FCSTD DOCUMENT  (FreeCAD 0.20R29177 (Git))
Label: miniXY-Assembly
License: All rights reserved
LicenseURL: http://en.wikipedia.org/wiki/All_rights_reserved
objects: App::Link×28, PartDesign::CoordinateSystem×9, Part::FeaturePython×5, App::DocumentObjectGroup×3, App::Part×2, App::FeaturePython×1
note: 14 computed .brp shape members not serialized (recipe doc carries the construction recipe); baked Part::Feature solids carry a one-line shape summary decoded from their .brp
EXTERNAL_REF file=miniXY-Frame.FCStd obj=LCS_TopPanelOrigin
EXTERNAL_REF file=miniXY-Frame.FCStd obj=Part004
EXTERNAL_REF file=../../AppData/Local/Temp/FreeCAD/Cache/FreeCAD_Doc_34dbc569-a2dc-46c2-a682-62368ed8909b_da39a3_1616 obj=Assembly
EXTERNAL_REF file=MGN9.FCStd obj=Assembly
EXTERNAL_REF file=../../AppData/Local/Temp/FreeCAD/Cache/FreeCAD_Doc_1c5c6fb1-aa33-4595-8116-cb341c517bc9_da39a3_1616 obj=Assembly
EXTERNAL_REF file=miniXY-Frame.FCStd obj=LCS_ZLeftRailOrigin
EXTERNAL_REF file=../../AppData/Local/Temp/FreeCAD/Cache/FreeCAD_Doc_671cf0bc-0ead-4e0d-b06c-74b64cb66649_da39a3_1616 obj=LCS_Origin
EXTERNAL_REF file=../../AppData/Local/Temp/FreeCAD/Cache/FreeCAD_Doc_671cf0bc-0ead-4e0d-b06c-74b64cb66649_da39a3_1616 obj=Assembly
EXTERNAL_REF file=miniXY-Frame.FCStd obj=LCS_ZRightRailOrigin
EXTERNAL_REF file=../../AppData/Local/Temp/FreeCAD/Cache/FreeCAD_Doc_395b4d48-7136-408e-876a-f83ec305f416_da39a3_1616 obj=LCS_Origin
EXTERNAL_REF file=../../AppData/Local/Temp/FreeCAD/Cache/FreeCAD_Doc_395b4d48-7136-408e-876a-f83ec305f416_da39a3_1616 obj=Assembly
EXTERNAL_REF file=../../AppData/Local/Temp/FreeCAD/Cache/FreeCAD_Doc_015ec990-f264-4db3-840c-f19af65eb745_da39a3_1616 obj=Assembly
EXTERNAL_REF file=miniXY-XYCarriage.FCStd obj=LCS_Origin
EXTERNAL_REF file=miniXY-XYCarriage.FCStd obj=Model
EXTERNAL_REF file=Drive.FCStd obj=LCS_PullyW6T20_Origin
EXTERNAL_REF file=miniXY-XYCarriage.FCStd obj=LCS_LeftOuterIdlerPosition
EXTERNAL_REF file=Drive.FCStd obj=Part001
EXTERNAL_REF file=miniXY-XYCarriage.FCStd obj=LCS_LeftInnerIdlerPosition
EXTERNAL_REF file=miniXY-XYCarriage.FCStd obj=LCS_RightOuterIdlerPosition
EXTERNAL_REF file=miniXY-XYCarriage.FCStd obj=LCS_RightInnerIdlerPosition
EXTERNAL_REF file=miniXY-Frame.FCStd obj=LCS_StepperMountLeft
EXTERNAL_REF file=miniXY-Frame.FCStd obj=StepperMountLeft
EXTERNAL_REF file=miniXY-Frame.FCStd obj=LCS_StepperMountRightOrigin
EXTERNAL_REF file=miniXY-Frame.FCStd obj=Part015
EXTERNAL_REF file=Drive.FCStd obj=LCS_Nema17_Origin
EXTERNAL_REF file=miniXY-Frame.FCStd obj=LCS_StepperLeftOrigin
EXTERNAL_REF file=Drive.FCStd obj=Part
EXTERNAL_REF file=miniXY-Frame.FCStd obj=LCS_StepperRightOrigin
EXTERNAL_REF file=Drive.FCStd obj=LCS_DriveW6T20
EXTERNAL_REF file=miniXY-Frame.FCStd obj=LCS_DrivePullyLeftOrigin
EXTERNAL_REF file=Drive.FCStd obj=Part002
EXTERNAL_REF file=miniXY-Frame.FCStd obj=LCS_DrivePullyRightOrigin
EXTERNAL_REF file=miniXY-Frame.FCStd obj=LCS_IdlerLeftRearOrigin
EXTERNAL_REF file=miniXY-Frame.FCStd obj=LCS_IdlerLeftFrontOrigin
EXTERNAL_REF file=miniXY-Frame.FCStd obj=LCS_IdlerRightRearOrigin
EXTERNAL_REF file=miniXY-Frame.FCStd obj=LCS_IdlerRightFrontOrigin
EXTERNAL_REF file=miniXY-Frame.FCStd obj=LCS_IdlerStepperLeftOrigin
EXTERNAL_REF file=miniXY-Frame.FCStd obj=LCS_IdlerStepperRightOrigin
EXTERNAL_REF file=miniXY-Frame.FCStd obj=LCS_LeftPullyMountOrigin
EXTERNAL_REF file=miniXY-Frame.FCStd obj=LeftPullyMount
EXTERNAL_REF file=miniXY-Frame.FCStd obj=LCS_RightPullyMountOrigin
EXTERNAL_REF file=miniXY-Frame.FCStd obj=Part017
EXTERNAL_REF file=miniXY-Frame.FCStd obj=LCS_LeftPanelOrigin001
EXTERNAL_REF file=miniXY-Frame.FCStd obj=LeftPanel001
EXTERNAL_REF file=miniXY-Frame.FCStd obj=LCS_RightPanelOrigin
EXTERNAL_REF file=miniXY-Frame.FCStd obj=Part007
EXTERNAL_REF file=miniXY-Frame.FCStd obj=LCS_UpperBracketRightOrigin
EXTERNAL_REF file=miniXY-Frame.FCStd obj=Part016
EXTERNAL_REF file=miniXY-ZDrive.FCStd obj=LCS_Origin
EXTERNAL_REF file=miniXY-ZDrive.FCStd obj=Model
EXTERNAL_REF file=miniXY-PrintBed.FCStd obj=LCS_Origin
EXTERNAL_REF file=miniXY-PrintBed.FCStd obj=Model
EXTERNAL_REF file=E3D-V6-Mockup.FCStd obj=LCS_V6HotEndOrigin
EXTERNAL_REF file=E3D-V6-Mockup.FCStd obj=Part

FEATURE [PartDesign::CoordinateSystem] LCS_Origin
  AttacherType = Attacher::AttachEngine3D
  MapMode = 2
  Support = -> [X_Axis]
FEATURE [App::DocumentObjectGroup] Constraints
FEATURE [App::FeaturePython] Variables  # WARN: FeaturePython — macro-defined, semantics opaque (R4)
  GantorySpacing = 200
  PositionX = 0
  PositionY = 0
  PositionZ = -63
  Type = App::PropertyContainer
FEATURE [App::DocumentObjectGroup] Configurations
FEATURE [App::Link] TopPanel
  AssemblyType = Part::Link
  AttachedBy = #LCS_TopPanelOrigin
  AttachedTo = Parent Assembly#LCS_Origin
  LinkPlacement = pos=(0,0,0) rot=(0,-1,0;3.14159rad)
  LinkedObject = -> <external miniXY-Frame.FCStd>#Part004
  Placement = pos=(0,0,0) rot=(0,-1,0;3.14159rad)
  SolverId = Asm4EE
  expr: Placement = LCS_Origin.Placement * AttachmentOffset * miniXY_Axis#LCS_TopPanelOrigin.Placement ^ -1
FEATURE [PartDesign::CoordinateSystem] LCS_GantoryOrigin
  AttacherType = Attacher::AttachEngine3D
  MapMode = 2
  Support = -> [X_Axis001]
FEATURE [Part::FeaturePython] MGN9_Y_Left  # link proxy (typed FeaturePython)
  AttachedBy = #LCS_Origin
  AttachedTo = GantoryPositions#LCS_YLeftRailOrigin
  Length = 175
  LinkedObject = -> <external ../../AppData/Local/Temp/FreeCAD/Cache/FreeCAD_Doc_34dbc569-a2dc-46c2-a682-62368ed8909b_da39a3_1616>#Assembly
  Placement = pos=(-100,2.11e-14,-10) rot=(0.707107,0.707107,0;3.14159rad)
  Position = 0
  SolverId = Asm4EE
  SourceObject = -> <external MGN9.FCStd>#Assembly
  expr: Placement = GantoryPositions.Placement * LCS_YLeftRailOrigin.Placement * AttachmentOffset * varTmpDoc_1#LCS_Origin.Placement ^ -1
  expr: Position = <<Variables>>.PositionY
FEATURE [Part::FeaturePython] MGN9_Y_Right  # link proxy (typed FeaturePython)
  AttachedBy = #LCS_Origin
  AttachedTo = GantoryPositions#LCS_YRightRailOrigin
  Length = 175
  LinkedObject = -> <external ../../AppData/Local/Temp/FreeCAD/Cache/FreeCAD_Doc_1c5c6fb1-aa33-4595-8116-cb341c517bc9_da39a3_1616>#Assembly
  Placement = pos=(100,-2.33e-14,-10) rot=(0.707107,0.707107,0;3.14159rad)
  Position = 0
  SolverId = Asm4EE
  SourceObject = -> <external MGN9.FCStd>#Assembly
  expr: Placement = GantoryPositions.Placement * LCS_YRightRailOrigin.Placement * AttachmentOffset * varTmpDoc_2#LCS_Origin.Placement ^ -1
  expr: Position = <<Variables>>.PositionY
FEATURE [Part::FeaturePython] MGN9_Z_Left  # link proxy (typed FeaturePython)
  AttachedBy = #LCS_Origin
  AttachedTo = LeftPanel#LCS_ZLeftRailOrigin
  Length = 175
  LinkedObject = -> <external ../../AppData/Local/Temp/FreeCAD/Cache/FreeCAD_Doc_671cf0bc-0ead-4e0d-b06c-74b64cb66649_da39a3_1616>#Assembly
  Placement = pos=(-110,-15,-160) rot=(0,1,0;1.5708rad)
  Position = -63
  SolverId = Asm4EE
  SourceObject = -> <external MGN9.FCStd>#Assembly
  expr: Placement = LeftPanel.Placement * miniXY_Axis#LCS_ZLeftRailOrigin.Placement * AttachmentOffset * varTmpDoc_3#LCS_Origin.Placement ^ -1
  expr: Position = <<Variables>>.PositionZ
FEATURE [Part::FeaturePython] MGN9_Z_Right  # link proxy (typed FeaturePython)
  AttachedBy = #LCS_Origin
  AttachedTo = RightPanel#LCS_ZRightRailOrigin
  Length = 175
  LinkedObject = -> <external ../../AppData/Local/Temp/FreeCAD/Cache/FreeCAD_Doc_395b4d48-7136-408e-876a-f83ec305f416_da39a3_1616>#Assembly
  Placement = pos=(110,-15,-160) rot=(-0.707107,0,0.707107;3.14159rad)
  Position = -63
  SolverId = Asm4EE
  SourceObject = -> <external MGN9.FCStd>#Assembly
  expr: Placement = RightPanel.Placement * miniXY_Axis#LCS_ZRightRailOrigin.Placement * AttachmentOffset * varTmpDoc_4#LCS_Origin.Placement ^ -1
  expr: Position = <<Variables>>.PositionZ
FEATURE [Part::FeaturePython] MGN9_X  # link proxy (typed FeaturePython)
  AttachedBy = #LCS_Origin
  AttachedTo = GantoryPositions#LCS_XRailOrigin
  Length = 175
  LinkedObject = -> <external ../../AppData/Local/Temp/FreeCAD/Cache/FreeCAD_Doc_015ec990-f264-4db3-840c-f19af65eb745_da39a3_1616>#Assembly
  Placement = pos=(0,0,-20) rot=(0,0,1;0rad)
  Position = 0
  SolverId = Asm4EE
  SourceObject = -> <external MGN9.FCStd>#Assembly
  expr: Placement = GantoryPositions.Placement * LCS_XRailOrigin.Placement * AttachmentOffset * varTmpDoc_5#LCS_Origin.Placement ^ -1
  expr: Position = <<Variables>>.PositionX
FEATURE [App::Link] GantoryPositions  label="GantoryPositions001"
  AssemblyType = Part::Link
  AttachedBy = #LCS_GantoryOrigin
  AttachedTo = Parent Assembly#LCS_Origin
  LinkedObject = -> Part
  SolverId = Asm4EE
  expr: Placement = LCS_Origin.Placement * AttachmentOffset * LCS_GantoryOrigin.Placement ^ -1
FEATURE [PartDesign::CoordinateSystem] LCS_XRailOrigin
  AttacherType = Attacher::AttachEngine3D
  AttachmentOffset = pos=(0,0,-20) rot=(0,0,1;0rad)
  MapMode = 2
  Placement = pos=(0,0,-20) rot=(0,0,1;0rad)
  Support = -> [X_Axis001]
  expr: .AttachmentOffset.Base.y = <<Variables>>.PositionY
FEATURE [PartDesign::CoordinateSystem] LCS_YLeftRailOrigin
  AttacherType = Attacher::AttachEngine3D
  AttachmentOffset = pos=(0,-100,10) rot=(0,0,1;0rad)
  MapMode = 3
  Placement = pos=(-100,2.11e-14,-10) rot=(0.707107,0.707107,0;3.14159rad)
  Support = -> [Y_Axis001]
  expr: .AttachmentOffset.Base.y = -<<Variables>>.GantorySpacing / 2
FEATURE [PartDesign::CoordinateSystem] LCS_YRightRailOrigin
  AttacherType = Attacher::AttachEngine3D
  AttachmentOffset = pos=(0,100,10) rot=(0,0,1;0rad)
  MapMode = 3
  Placement = pos=(100,-2.33e-14,-10) rot=(0.707107,0.707107,0;3.14159rad)
  Support = -> [Y_Axis001]
  expr: .AttachmentOffset.Base.y = <<Variables>>.GantorySpacing / 2
FEATURE [App::Link] XYCarriage
  AttachedBy = #LCS_Origin
  AttachedTo = GantoryPositions#LCS_XYCarriageOrigin
  LinkPlacement = pos=(0,0,-20) rot=(1,0,0;3.14159rad)
  LinkedObject = -> <external miniXY-XYCarriage.FCStd>#Model
  Placement = pos=(0,0,-20) rot=(1,0,0;3.14159rad)
  SolverId = Asm4EE
  expr: Placement = GantoryPositions.Placement * LCS_XYCarriageOrigin.Placement * AttachmentOffset * miniXY_XYCarriage#LCS_Origin.Placement ^ -1
FEATURE [PartDesign::CoordinateSystem] LCS_XYCarriageOrigin
  AttacherType = Attacher::AttachEngine3D
  AttachmentOffset = pos=(0,0,-20) rot=(1,0,0;3.14159rad)
  MapMode = 2
  Placement = pos=(0,0,-20) rot=(1,0,0;3.14159rad)
  Support = -> [X_Axis001]
  expr: .AttachmentOffset.Base.y = <<Variables>>.PositionY
FEATURE [App::Link] IdlerCarriageLeftOuter
  AssemblyType = Part::Link
  AttachedBy = #LCS_PullyW6T20_Origin
  AttachedTo = XYCarriage#LCS_LeftOuterIdlerPosition
  LinkPlacement = pos=(-100,-1.4e-15,-31.75) rot=(1,0,0;3.14159rad)
  LinkedObject = -> <external Drive.FCStd>#Part001
  Placement = pos=(-100,-1.4e-15,-31.75) rot=(1,0,0;3.14159rad)
  SolverId = Asm4EE
  expr: Placement = XYCarriage.Placement * miniXY_XYCarriage#LCS_LeftOuterIdlerPosition.Placement * AttachmentOffset * Drive#LCS_PullyW6T20_Origin.Placement ^ -1
FEATURE [App::Link] IdlerCarriageLeftInner
  AssemblyType = Part::Link
  AttachedBy = #LCS_PullyW6T20_Origin
  AttachedTo = XYCarriage#LCS_LeftInnerIdlerPosition
  LinkPlacement = pos=(-87.27,-2.6e-15,-41.25) rot=(1,0,0;3.14159rad)
  LinkedObject = -> <external Drive.FCStd>#Part001
  Placement = pos=(-87.27,-2.6e-15,-41.25) rot=(1,0,0;3.14159rad)
  SolverId = Asm4EE
  expr: Placement = XYCarriage.Placement * miniXY_XYCarriage#LCS_LeftInnerIdlerPosition.Placement * AttachmentOffset * Drive#LCS_PullyW6T20_Origin.Placement ^ -1
FEATURE [App::Link] IdlerCarriageRightOuter
  AssemblyType = Part::Link
  AttachedBy = #LCS_PullyW6T20_Origin
  AttachedTo = XYCarriage#LCS_RightOuterIdlerPosition
  LinkPlacement = pos=(100,-2.6e-15,-41.25) rot=(1,0,0;3.14159rad)
  LinkedObject = -> <external Drive.FCStd>#Part001
  Placement = pos=(100,-2.6e-15,-41.25) rot=(1,0,0;3.14159rad)
  SolverId = Asm4EE
  expr: Placement = XYCarriage.Placement * miniXY_XYCarriage#LCS_RightOuterIdlerPosition.Placement * AttachmentOffset * Drive#LCS_PullyW6T20_Origin.Placement ^ -1
FEATURE [App::Link] IdlerCarriageRightInner
  AssemblyType = Part::Link
  AttachedBy = #LCS_PullyW6T20_Origin
  AttachedTo = XYCarriage#LCS_RightInnerIdlerPosition
  LinkPlacement = pos=(87.27,-1.4e-15,-31.75) rot=(1,0,0;3.14159rad)
  LinkedObject = -> <external Drive.FCStd>#Part001
  Placement = pos=(87.27,-1.4e-15,-31.75) rot=(1,0,0;3.14159rad)
  SolverId = Asm4EE
  expr: Placement = XYCarriage.Placement * miniXY_XYCarriage#LCS_RightInnerIdlerPosition.Placement * AttachmentOffset * Drive#LCS_PullyW6T20_Origin.Placement ^ -1
FEATURE [App::Link] StepperMountLeft
  AssemblyType = Part::Link
  AttachedBy = #LCS_StepperMountLeft
  AttachedTo = Parent Assembly#LCS_Origin
  LinkPlacement = pos=(-100,100,-46) rot=(-1,0,0;3.14159rad)
  LinkedObject = -> <external miniXY-Frame.FCStd>#StepperMountLeft
  Placement = pos=(-100,100,-46) rot=(-1,0,0;3.14159rad)
  SolverId = Asm4EE
  expr: Placement = LCS_Origin.Placement * AttachmentOffset * miniXY_Axis#LCS_StepperMountLeft.Placement ^ -1
FEATURE [App::Link] StepperMountRight
  AssemblyType = Part::Link
  AttachedBy = #LCS_StepperMountRightOrigin
  AttachedTo = Parent Assembly#LCS_Origin
  LinkPlacement = pos=(100,100,-46) rot=(-1,0,0;3.14159rad)
  LinkedObject = -> <external miniXY-Frame.FCStd>#Part015
  Placement = pos=(100,100,-46) rot=(-1,0,0;3.14159rad)
  SolverId = Asm4EE
  expr: Placement = LCS_Origin.Placement * AttachmentOffset * miniXY_Axis#LCS_StepperMountRightOrigin.Placement ^ -1
FEATURE [App::Link] StepperLeft
  AssemblyType = Part::Link
  AttachedBy = #LCS_Nema17_Origin
  AttachedTo = StepperMountLeft#LCS_StepperLeftOrigin
  LinkPlacement = pos=(-100,143.5,-51) rot=(0,0,1;0rad)
  LinkedObject = -> <external Drive.FCStd>#Part
  Placement = pos=(-100,143.5,-51) rot=(0,0,1;0rad)
  SolverId = Asm4EE
  expr: Placement = StepperMountLeft.Placement * miniXY_Axis#LCS_StepperLeftOrigin.Placement * AttachmentOffset * Drive#LCS_Nema17_Origin.Placement ^ -1
FEATURE [App::Link] StepperRight
  AssemblyType = Part::Link
  AttachedBy = #LCS_Nema17_Origin
  AttachedTo = StepperMountRight#LCS_StepperRightOrigin
  LinkPlacement = pos=(100,143.5,-51) rot=(0,0,1;0rad)
  LinkedObject = -> <external Drive.FCStd>#Part
  Placement = pos=(100,143.5,-51) rot=(0,0,1;0rad)
  SolverId = Asm4EE
  expr: Placement = StepperMountRight.Placement * miniXY_Axis#LCS_StepperRightOrigin.Placement * AttachmentOffset * Drive#LCS_Nema17_Origin.Placement ^ -1
FEATURE [App::Link] DrivePullyLeft
  AssemblyType = Part::Link
  AttachedBy = #LCS_DriveW6T20
  AttachedTo = StepperMountLeft#LCS_DrivePullyLeftOrigin
  LinkPlacement = pos=(-100,143.5,-41.25) rot=(-1,0,0;3.14159rad)
  LinkedObject = -> <external Drive.FCStd>#Part002
  Placement = pos=(-100,143.5,-41.25) rot=(-1,0,0;3.14159rad)
  SolverId = Asm4EE
  expr: Placement = StepperMountLeft.Placement * miniXY_Axis#LCS_DrivePullyLeftOrigin.Placement * AttachmentOffset * Drive#LCS_DriveW6T20.Placement ^ -1
FEATURE [App::Link] DrivePullyRight
  AssemblyType = Part::Link
  AttachedBy = #LCS_DriveW6T20
  AttachedTo = StepperMountRight#LCS_DrivePullyRightOrigin
  LinkPlacement = pos=(100,143.5,-31.75) rot=(0,0,-1;1.5708rad)
  LinkedObject = -> <external Drive.FCStd>#Part002
  Placement = pos=(100,143.5,-31.75) rot=(0,0,-1;1.5708rad)
  SolverId = Asm4EE
  expr: Placement = StepperMountRight.Placement * miniXY_Axis#LCS_DrivePullyRightOrigin.Placement * AttachmentOffset * Drive#LCS_DriveW6T20.Placement ^ -1
FEATURE [App::Link] IdlerLeftRear
  AttachedBy = #LCS_PullyW6T20_Origin
  AttachedTo = StepperMountLeft#LCS_IdlerLeftRearOrigin
  LinkPlacement = pos=(-100,100,-31.75) rot=(0,0,-1;1.5708rad)
  LinkedObject = -> <external Drive.FCStd>#Part001
  Placement = pos=(-100,100,-31.75) rot=(0,0,-1;1.5708rad)
  SolverId = Asm4EE
  expr: Placement = StepperMountLeft.Placement * miniXY_Axis#LCS_IdlerLeftRearOrigin.Placement * AttachmentOffset * Drive#LCS_PullyW6T20_Origin.Placement ^ -1
FEATURE [App::Link] IdlerLeftFront
  AttachedBy = #LCS_PullyW6T20_Origin
  AttachedTo = LeftPullyMount#LCS_IdlerLeftFrontOrigin
  LinkPlacement = pos=(-100,-100,-41.25) rot=(0,0,1;1.5708rad)
  LinkedObject = -> <external Drive.FCStd>#Part001
  Placement = pos=(-100,-100,-41.25) rot=(0,0,1;1.5708rad)
  SolverId = Asm4EE
  expr: Placement = LeftPullyMount.Placement * miniXY_Axis#LCS_IdlerLeftFrontOrigin.Placement * AttachmentOffset * Drive#LCS_PullyW6T20_Origin.Placement ^ -1
FEATURE [App::Link] IdlerRightRear
  AssemblyType = Part::Link
  AttachedBy = #LCS_PullyW6T20_Origin
  AttachedTo = StepperMountRight#LCS_IdlerRightRearOrigin
  LinkPlacement = pos=(100,100,-41.25) rot=(0,0,-1;1.5708rad)
  LinkedObject = -> <external Drive.FCStd>#Part001
  Placement = pos=(100,100,-41.25) rot=(0,0,-1;1.5708rad)
  SolverId = Asm4EE
  expr: Placement = StepperMountRight.Placement * miniXY_Axis#LCS_IdlerRightRearOrigin.Placement * AttachmentOffset * Drive#LCS_PullyW6T20_Origin.Placement ^ -1
FEATURE [App::Link] IdlerRightFront
  AttachedBy = #LCS_PullyW6T20_Origin
  AttachedTo = RightPullyMount#LCS_IdlerRightFrontOrigin
  LinkPlacement = pos=(100,-100,-31.75) rot=(0,0,1;1.5708rad)
  LinkedObject = -> <external Drive.FCStd>#Part001
  Placement = pos=(100,-100,-31.75) rot=(0,0,1;1.5708rad)
  SolverId = Asm4EE
  expr: Placement = RightPullyMount.Placement * miniXY_Axis#LCS_IdlerRightFrontOrigin.Placement * AttachmentOffset * Drive#LCS_PullyW6T20_Origin.Placement ^ -1
FEATURE [App::Link] IdlerLeftStepper
  AttachedBy = #LCS_PullyW6T20_Origin
  AttachedTo = StepperMountLeft#LCS_IdlerStepperLeftOrigin
  LinkPlacement = pos=(-87.27,112.73,-41.25) rot=(0,0,-1;1.5708rad)
  LinkedObject = -> <external Drive.FCStd>#Part001
  Placement = pos=(-87.27,112.73,-41.25) rot=(0,0,-1;1.5708rad)
  SolverId = Asm4EE
  expr: Placement = StepperMountLeft.Placement * miniXY_Axis#LCS_IdlerStepperLeftOrigin.Placement * AttachmentOffset * Drive#LCS_PullyW6T20_Origin.Placement ^ -1
FEATURE [App::Link] IdlerRightStepper
  AssemblyType = Part::Link
  AttachedBy = #LCS_PullyW6T20_Origin
  AttachedTo = StepperMountRight#LCS_IdlerStepperRightOrigin
  LinkPlacement = pos=(87.27,112.73,-31.75) rot=(0,0,-1;1.5708rad)
  LinkedObject = -> <external Drive.FCStd>#Part001
  Placement = pos=(87.27,112.73,-31.75) rot=(0,0,-1;1.5708rad)
  SolverId = Asm4EE
  expr: Placement = StepperMountRight.Placement * miniXY_Axis#LCS_IdlerStepperRightOrigin.Placement * AttachmentOffset * Drive#LCS_PullyW6T20_Origin.Placement ^ -1
FEATURE [App::Link] LeftPullyMount
  AssemblyType = Part::Link
  AttachedBy = #LCS_LeftPullyMountOrigin
  AttachedTo = Parent Assembly#LCS_Origin
  LinkPlacement = pos=(-100,-100,-60) rot=(0,-1,0;3.14159rad)
  LinkedObject = -> <external miniXY-Frame.FCStd>#LeftPullyMount
  Placement = pos=(-100,-100,-60) rot=(0,-1,0;3.14159rad)
  SolverId = Asm4EE
  expr: Placement = LCS_Origin.Placement * AttachmentOffset * miniXY_Axis#LCS_LeftPullyMountOrigin.Placement ^ -1
FEATURE [App::Link] RightPullyMount
  AssemblyType = Part::Link
  AttachedBy = #LCS_RightPullyMountOrigin
  AttachedTo = Parent Assembly#LCS_Origin
  LinkPlacement = pos=(100,-100,-60) rot=(0,-1,0;3.14159rad)
  LinkedObject = -> <external miniXY-Frame.FCStd>#Part017
  Placement = pos=(100,-100,-60) rot=(0,-1,0;3.14159rad)
  SolverId = Asm4EE
  expr: Placement = LCS_Origin.Placement * AttachmentOffset * miniXY_Axis#LCS_RightPullyMountOrigin.Placement ^ -1
FEATURE [App::Link] LeftPanel
  AssemblyType = Part::Link
  AttachedBy = #LCS_LeftPanelOrigin001
  AttachedTo = Parent Assembly#LCS_Origin
  LinkPlacement = pos=(-110,0,-60) rot=(0,1,0;1.5708rad)
  LinkedObject = -> <external miniXY-Frame.FCStd>#LeftPanel001
  Placement = pos=(-110,0,-60) rot=(0,1,0;1.5708rad)
  SolverId = Asm4EE
  expr: Placement = LCS_Origin.Placement * AttachmentOffset * miniXY_Axis#LCS_LeftPanelOrigin001.Placement ^ -1
FEATURE [App::Link] RightPanel
  AssemblyType = Part::Link
  AttachedBy = #LCS_RightPanelOrigin
  AttachedTo = Parent Assembly#LCS_Origin
  LinkPlacement = pos=(110,0,-60) rot=(0,-1,0;1.5708rad)
  LinkedObject = -> <external miniXY-Frame.FCStd>#Part007
  Placement = pos=(110,0,-60) rot=(0,-1,0;1.5708rad)
  SolverId = Asm4EE
  expr: Placement = LCS_Origin.Placement * AttachmentOffset * miniXY_Axis#LCS_RightPanelOrigin.Placement ^ -1
FEATURE [App::Link] UpperBracket
  AssemblyType = Part::Link
  AttachedBy = #LCS_UpperBracketRightOrigin
  AttachedTo = Parent Assembly#LCS_Origin
  LinkPlacement = pos=(0,110,-59) rot=(1,0,0;1.5708rad)
  LinkedObject = -> <external miniXY-Frame.FCStd>#Part016
  Placement = pos=(0,110,-59) rot=(1,0,0;1.5708rad)
  SolverId = Asm4EE
  expr: Placement = LCS_Origin.Placement * AttachmentOffset * miniXY_Axis#LCS_UpperBracketRightOrigin.Placement ^ -1
FEATURE [PartDesign::CoordinateSystem] LCS_ZDriveShaftOrigin
  AttacherType = Attacher::AttachEngine3D
  AttachmentOffset = pos=(0,-2.27,-255) rot=(0,0,1;0rad)
  MapMode = 2
  Placement = pos=(0,-2.27,-255) rot=(0,0,1;0rad)
  Support = -> [X_Axis001]
  expr: .AttachmentOffset.Base.y = 12.73 - 15
FEATURE [App::Link] ZDriveShaft
  AttachedBy = #LCS_Origin
  AttachedTo = GantoryPositions#LCS_ZDriveShaftOrigin
  LinkPlacement = pos=(0,-2.27,-255) rot=(0,0,1;0rad)
  LinkedObject = -> <external miniXY-ZDrive.FCStd>#Model
  Placement = pos=(0,-2.27,-255) rot=(0,0,1;0rad)
  SolverId = Asm4EE
  expr: Placement = GantoryPositions.Placement * LCS_ZDriveShaftOrigin.Placement * AttachmentOffset * miniXY_ZDrive#LCS_Origin.Placement ^ -1
FEATURE [App::Link] miniXY_PrintBed  label="PrintBed"
  AttachedBy = #LCS_Origin
  AttachedTo = GantoryPositions#LCS_PrintBedOrigin
  LinkPlacement = pos=(0,-15,-97) rot=(0,0,1;0rad)
  LinkedObject = -> <external miniXY-PrintBed.FCStd>#Model
  Placement = pos=(0,-15,-97) rot=(0,0,1;0rad)
  SolverId = Asm4EE
  expr: Placement = GantoryPositions.Placement * LCS_PrintBedOrigin.Placement * AttachmentOffset * miniXY_PrintBed#LCS_Origin.Placement ^ -1
FEATURE [PartDesign::CoordinateSystem] LCS_PrintBedOrigin
  AttacherType = Attacher::AttachEngine3D
  AttachmentOffset = pos=(0,-15,-97) rot=(0,0,1;0rad)
  MapMode = 2
  Placement = pos=(0,-15,-97) rot=(0,0,1;0rad)
  Support = -> [X_Axis001]
  expr: .AttachmentOffset.Base.z = -160 - Variables.PositionZ
FEATURE [App::Link] StepperZ
  LinkPlacement = pos=(45,-40,-249) rot=(0,1,0;1.5708rad)
  LinkedObject = -> <external Drive.FCStd>#Part
  Placement = pos=(45,-40,-249) rot=(0,1,0;1.5708rad)
FEATURE [PartDesign::CoordinateSystem] LCS_V6HotEndOrigin
  AttacherType = Attacher::AttachEngine3D
  AttachmentOffset = pos=(0,-20,-15) rot=(0,0,1;0rad)
  MapMode = 2
  Placement = pos=(0,-20,-15) rot=(0,0,1;0rad)
  Support = -> [X_Axis001]
  expr: .AttachmentOffset.Base.x = <<Variables>>.PositionX
  expr: .AttachmentOffset.Base.y = -20 + <<Variables>>.PositionY
FEATURE [App::Part] Part  label="GantoryPositions"
  Group = -> [LCS_GantoryOrigin,LCS_XRailOrigin,LCS_YLeftRailOrigin,LCS_YRightRailOrigin,LCS_XYCarriageOrigin,LCS_ZDriveShaftOrigin,LCS_PrintBedOrigin,LCS_V6HotEndOrigin]
  Origin = -> Origin001
FEATURE [App::DocumentObjectGroup] Parts
  Group = -> [Part]
FEATURE [App::Link] V6HotEnd
  AssemblyType = Part::Link
  AttachedBy = #LCS_V6HotEndOrigin
  AttachedTo = GantoryPositions#LCS_V6HotEndOrigin
  LinkPlacement = pos=(0,-20,-15) rot=(0,0,1;0rad)
  LinkedObject = -> <external E3D-V6-Mockup.FCStd>#Part
  Placement = pos=(0,-20,-15) rot=(0,0,1;0rad)
  SolverId = Asm4EE
  expr: Placement = GantoryPositions.Placement * LCS_V6HotEndOrigin.Placement * AttachmentOffset * E3D_V6_Mockup#LCS_V6HotEndOrigin.Placement ^ -1
FEATURE [App::Part] Model
  AssemblyType = Part::Link
  Group = -> [LCS_Origin,Constraints,Variables,Configurations,TopPanel,MGN9_Y_Left,MGN9_Y_Right,MGN9_Z_Left,MGN9_Z_Right,MGN9_X,GantoryPositions,XYCarriage,IdlerCarriageLeftOuter,IdlerCarriageLeftInner,IdlerCarriageRightOuter,IdlerCarriageRightInner,StepperMountLeft,StepperMountRight,StepperLeft,StepperRight,DrivePullyLeft,DrivePullyRight,IdlerLeftRear,IdlerLeftFront,IdlerRightRear,IdlerRightFront,+11 more]
  Origin = -> Origin
  Type = Assembly

RESOLVED EXTERNAL PARTS (link-assembly join: the EXTERNAL_REF files above that resolve inside this repo's crawl, each included once):
---- part Drive.FCStd = doc fcstd_4fe1558333d0 ----
FCSTD DOCUMENT  (FreeCAD 0.20R29177 (Git))
Label: Drive
License: All rights reserved
LicenseURL: http://en.wikipedia.org/wiki/All_rights_reserved
objects: PartDesign::Body×7, PartDesign::CoordinateSystem×7, App::Part×4, PartDesign::AdditiveBox×3, PartDesign::Chamfer×3, PartDesign::AdditiveCylinder×3, Sketcher::SketchObject×3, PartDesign::Revolution×2, PartDesign::AdditiveCone×2, PartDesign::Hole×1, PartDesign::SubtractiveCylinder×1
note: 47 computed .brp shape members not serialized (recipe doc carries the construction recipe); baked Part::Feature solids carry a one-line shape summary decoded from their .brp

FEATURE [PartDesign::AdditiveBox] Box
  AttacherType = Attacher::AttachEngine3D
  AttachmentOffset = pos=(-21,-21,0) rot=(0,0,1;0rad)
  Height = 8
  Length = 42
  MapMode = 2
  Placement = pos=(21,-21,0) rot=(0,1,0;3.14159rad)
  Support = -> [XY_Plane001]
  Width = 42
FEATURE [PartDesign::Chamfer] Chamfer
  Angle = 45
  Base = -> Box [Edge1,Edge3,Edge5,Edge7]
  BaseFeature = -> Box
  ChamferType = 0
  FlipDirection = false
  Placement = pos=(21,-21,0) rot=(0,1,0;3.14159rad)
  Size = 4
  Size2 = 1
  SupportTransform = false
  UseAllEdges = false
FEATURE [PartDesign::AdditiveBox] Box001
  AttacherType = Attacher::AttachEngine3D
  AttachmentOffset = pos=(-21,-21,0) rot=(0,0,1;0rad)
  Height = 20
  Length = 42
  MapMode = 2
  Placement = pos=(21,-21,0) rot=(0,1,0;3.14159rad)
  Support = -> [XY_Plane002]
  Width = 42
FEATURE [PartDesign::Chamfer] Chamfer001
  Angle = 45
  Base = -> Box001 [Edge1,Edge3,Edge5,Edge7]
  BaseFeature = -> Box001
  ChamferType = 0
  FlipDirection = false
  Placement = pos=(21,-21,0) rot=(0,1,0;3.14159rad)
  Size = 4
  Size2 = 1
  SupportTransform = false
  UseAllEdges = false
FEATURE [PartDesign::Body] Body001
  Group = -> [Box001,Chamfer001]
  Origin = -> Origin002
  Placement = pos=(0,0,-8) rot=(0,0,1;0rad)
  Tip = -> Chamfer001
FEATURE [PartDesign::AdditiveBox] Box002
  AttacherType = Attacher::AttachEngine3D
  AttachmentOffset = pos=(-21,-21,0) rot=(0,0,1;0rad)
  Height = 9
  Length = 42
  MapMode = 5
  Placement = pos=(21,-21,0) rot=(0,1,0;3.14159rad)
  Support = -> [XY_Plane003]
  Width = 42
FEATURE [PartDesign::Chamfer] Chamfer002
  Angle = 45
  Base = -> Box002 [Edge1,Edge3,Edge5,Edge7]
  BaseFeature = -> Box002
  ChamferType = 0
  FlipDirection = false
  Placement = pos=(21,-21,0) rot=(0,1,0;3.14159rad)
  Size = 4
  Size2 = 1
  SupportTransform = false
  UseAllEdges = false
FEATURE [PartDesign::Body] Body002
  Group = -> [Box002,Chamfer002]
  Origin = -> Origin003
  Placement = pos=(0,0,-28) rot=(0,0,1;0rad)
  Tip = -> Chamfer002
FEATURE [PartDesign::AdditiveCylinder] Cylinder
  Angle = 360
  AttacherType = Attacher::AttachEngine3D
  BaseFeature = -> Chamfer
  FirstAngle = 0
  Height = 2
  MapMode = 2
  Radius = 11
  SecondAngle = 0
  Support = -> [XY_Plane001]
FEATURE [PartDesign::AdditiveCylinder] Cylinder001
  Angle = 360
  AttacherType = Attacher::AttachEngine3D
  AttachmentOffset = pos=(0,0,2) rot=(0,0,1;0rad)
  FirstAngle = 0
  Height = 22
  MapMode = 5
  Placement = pos=(0,0,2) rot=(0,0,1;0rad)
  Radius = 2.5
  SecondAngle = 0
  Support = -> [XY_Plane004]
FEATURE [PartDesign::Body] Body003
  Group = -> [Cylinder001]
  Origin = -> Origin004
  Tip = -> Cylinder001
FEATURE [Sketcher::SketchObject] Sketch
  FullyConstrained = false
  MapMode = 5
  Support = -> [XY_Plane001]
  sketch-geometry (4):
    g0: Circle CenterX=-15.5 CenterY=15.3491 CenterZ=0 NormalX=0 NormalY=0 NormalZ=1 AngleXU=0 Radius=1.5
    g1: Circle CenterX=15.5 CenterY=15.3491 CenterZ=0 NormalX=0 NormalY=0 NormalZ=1 AngleXU=0 Radius=1.5
    g2: Circle CenterX=-15.5 CenterY=-15.3491 CenterZ=0 NormalX=0 NormalY=0 NormalZ=1 AngleXU=0 Radius=1.5
    g3: Circle CenterX=15.5 CenterY=-15.3491 CenterZ=0 NormalX=0 NormalY=0 NormalZ=1 AngleXU=0 Radius=1.5
  constraints (10):
    c: Horizontal(g0,g1)
    c: Vertical(g0,g2)
    c: Horizontal(g2,g3)
    c: Vertical(g1,g3)
    c: Symmetric(g0,g3,g-1)
    c: Equal(g0,g1)
    c: Equal(g0,g2)
    c: Equal(g0,g3)
    c: Diameter(g0) = 3
    c: DistanceX(g0,g1) = 31
FEATURE [PartDesign::Hole] Hole
  BaseFeature = -> Cylinder
  CustomThreadClearance = 0
  Depth = 5
  DepthType = 0
  Diameter = 3.4
  DrillForDepth = false
  DrillPoint = 1
  DrillPointAngle = 118
  HoleCutCountersinkAngle = 90
  HoleCutCustomValues = false
  HoleCutDepth = 0
  HoleCutDiameter = 6.1
  HoleCutType = 0
  ModelThread = false
  Profile = -> Sketch
  Tapered = false
  TaperedAngle = 90
  ThreadClass = 0
  ThreadDepth = 5
  ThreadDepthType = 0
  ThreadDirection = 0
  ThreadFit = 0
  ThreadSize = 9
  ThreadType = 1
  Threaded = false
  UseCustomThreadClearance = false
FEATURE [PartDesign::Body] Body
  Group = -> [Box,Chamfer,Cylinder,Sketch,Hole]
  Origin = -> Origin001
  Tip = -> Hole
FEATURE [Sketcher::SketchObject] Sketch001
  FullyConstrained = true
  MapMode = 5
  Placement = pos=(0,0,0) rot=(1,0,0;1.5708rad)
  Support = -> [XZ_Plane006]
  sketch-geometry (8):
    g0: LineSegment StartX=2.5 StartY=4.25 StartZ=0 EndX=2.5 EndY=-4.25 EndZ=0
    g1: LineSegment StartX=2.5 StartY=-4.25 StartZ=0 EndX=9 EndY=-4.25 EndZ=0
    g2: LineSegment StartX=9 StartY=-4.25 StartZ=0 EndX=9 EndY=-3.25 EndZ=0
    g3: LineSegment StartX=9 StartY=-3.25 StartZ=0 EndX=6.365 EndY=-3.25 EndZ=0
    g4: LineSegment StartX=6.365 StartY=-3.25 StartZ=0 EndX=6.365 EndY=3.25 EndZ=0
    g5: LineSegment StartX=6.365 StartY=3.25 StartZ=0 EndX=9 EndY=3.25 EndZ=0
    g6: LineSegment StartX=9 StartY=3.25 StartZ=0 EndX=9 EndY=4.25 EndZ=0
    g7: LineSegment StartX=9 StartY=4.25 StartZ=0 EndX=2.5 EndY=4.25 EndZ=0
  constraints (21):
    c: Coincident(g0,g1)
    c: Horizontal(g1)
    c: Coincident(g1,g2)
    c: Coincident(g2,g3)
    c: Coincident(g3,g4)
    c: Coincident(g4,g5)
    c: Horizontal(g5)
    c: Coincident(g5,g6)
    c: Coincident(g6,g7)
    c: Coincident(g7,g0)
    c: Horizontal(g7)
    c: Symmetric(g0,g0,g-1)
    c: Symmetric(g4,g3,g-1)
    c: Vertical(g6)
    c: Vertical(g2)
    c: Symmetric(g2,g5,g-1)
    c: DistanceX(g-1,g4) = 6.365
    c: DistanceX(g-1,g0) = 2.5
    c: DistanceY(g6,g6) = 1
    c: DistanceX(g-1,g6) = 9
    c: DistanceY(g3,g4) = 6.5
FEATURE [PartDesign::Revolution] Revolution
  Angle = 360
  Axis = (0,-2e-16,1)
  Base = (0,0,0)
  Placement = pos=(0,0,0) rot=(1,0,0;1.5708rad)
  Profile = -> Sketch001
  ReferenceAxis = -> Sketch001 [V_Axis]
FEATURE [PartDesign::Body] Body004
  Group = -> [Sketch001,Revolution]
  Origin = -> Origin006
  Tip = -> Revolution
FEATURE [PartDesign::CoordinateSystem] LCS_Nema17_Origin
  AttacherType = Attacher::AttachEngine3D
  MapMode = 2
  Support = -> [X_Axis]
FEATURE [App::Part] Part  label="Nema17"
  Group = -> [Body,Body001,Body002,Body003,LCS_Nema17_Origin]
  Origin = -> Origin
FEATURE [PartDesign::CoordinateSystem] LCS_PullyW6T20_Origin  label="LCS_IdlerW6T20_Origin"
  AttacherType = Attacher::AttachEngine3D
  MapMode = 2
  Support = -> [X_Axis005]
FEATURE [PartDesign::CoordinateSystem] LCS_PullyW6T20_Left  label="LCS_IdlerW6T20_Left"
  AttacherType = Attacher::AttachEngine3D
  AttachmentOffset = pos=(6.365,0,0) rot=(0,0,1;0rad)
  MapMode = 2
  Placement = pos=(6.365,0,0) rot=(0,0,1;0rad)
  Support = -> [LCS_PullyW6T20_Origin]
FEATURE [PartDesign::CoordinateSystem] LCS_PullyW6T20_Right  label="LCS_IdlerW6T20_Right"
  AttacherType = Attacher::AttachEngine3D
  AttachmentOffset = pos=(-6.365,0,0) rot=(0,0,1;0rad)
  MapMode = 2
  Placement = pos=(-6.365,0,0) rot=(0,0,1;0rad)
  Support = -> [LCS_PullyW6T20_Origin]
FEATURE [PartDesign::CoordinateSystem] LCS_PullyW6T20_Front  label="LCS_IdlerW6T20_Front"
  AttacherType = Attacher::AttachEngine3D
  AttachmentOffset = pos=(0,-6.365,0) rot=(0,0,1;0rad)
  MapMode = 2
  Placement = pos=(0,-6.365,0) rot=(0,0,1;0rad)
  Support = -> [LCS_PullyW6T20_Origin]
FEATURE [PartDesign::CoordinateSystem] LCS_PullyW6T20_Rear
  AttacherType = Attacher::AttachEngine3D
  AttachmentOffset = pos=(0,6.365,0) rot=(0,0,1;0rad)
  MapMode = 2
  Placement = pos=(0,6.365,0) rot=(0,0,1;0rad)
  Support = -> [LCS_PullyW6T20_Origin]
FEATURE [App::Part] Part001  label="IdlerW6T20"
  Group = -> [Body004,LCS_PullyW6T20_Origin,LCS_PullyW6T20_Left,LCS_PullyW6T20_Right,LCS_PullyW6T20_Front,LCS_PullyW6T20_Rear]
  Origin = -> Origin005
FEATURE [Sketcher::SketchObject] Sketch002
  FullyConstrained = true
  MapMode = 5
  Placement = pos=(0,0,0) rot=(1,0,0;1.5708rad)
  Support = -> [XZ_Plane008]
  sketch-geometry (8):
    g0: LineSegment StartX=2.5 StartY=4.9 StartZ=0 EndX=2.5 EndY=-11.1 EndZ=0
    g1: LineSegment StartX=2.5 StartY=-11.1 StartZ=0 EndX=8 EndY=-11.1 EndZ=0
    g2: LineSegment StartX=8 StartY=-11.1 StartZ=0 EndX=8 EndY=-3.6 EndZ=0
    g3: LineSegment StartX=8 StartY=-3.6 StartZ=0 EndX=6.365 EndY=-3.6 EndZ=0
    g4: LineSegment StartX=6.365 StartY=-3.6 StartZ=0 EndX=6.365 EndY=3.6 EndZ=0
    g5: LineSegment StartX=6.365 StartY=3.6 StartZ=0 EndX=8 EndY=3.6 EndZ=0
    g6: LineSegment StartX=8 StartY=3.6 StartZ=0 EndX=8 EndY=4.9 EndZ=0
    g7: LineSegment StartX=8 StartY=4.9 StartZ=0 EndX=2.5 EndY=4.9 EndZ=0
  constraints (23):
    c: Vertical(g0)
    c: Coincident(g0,g1)
    c: Coincident(g1,g2)
    c: Vertical(g2)
    c: Coincident(g2,g3)
    c: Coincident(g3,g4)
    c: Coincident(g4,g5)
    c: Horizontal(g5)
    c: Coincident(g5,g6)
    c: Vertical(g6)
    c: Coincident(g6,g7)
    c: Horizontal(g7)
    c: Coincident(g7,g0)
    c: Horizontal(g1)
    c: Horizontal(g3)
    c: DistanceX(g-1,g0) = 2.5
    c: DistanceY(g6,g6) = 1.3
    c: DistanceY(g4,g4) = 7.2
    c: DistanceY(g2,g2) = 7.5
    c: Symmetric(g4,g3,g-1)
    c: DistanceX(g-1,g4) = 6.365
    c: DistanceX(g-1,g1) = 8
    c: DistanceX(g-1,g6) = 8
FEATURE [PartDesign::Revolution] Revolution001
  Angle = 360
  Axis = (0,-2e-16,1)
  Base = (0,0,0)
  Placement = pos=(0,0,0) rot=(1,0,0;1.5708rad)
  Profile = -> Sketch002
  ReferenceAxis = -> Sketch002 [V_Axis]
FEATURE [PartDesign::Body] Body005
  Group = -> [Sketch002,Revolution001]
  Origin = -> Origin008
  Tip = -> Revolution001
FEATURE [PartDesign::CoordinateSystem] LCS_DriveW6T20
  AttacherType = Attacher::AttachEngine3D
  MapMode = 2
  Support = -> [X_Axis007]
FEATURE [App::Part] Part002  label="DriveW6T20"
  Group = -> [Body005,LCS_DriveW6T20]
  Origin = -> Origin007
FEATURE [PartDesign::AdditiveCylinder] Cylinder002
  Angle = 360
  AttacherType = Attacher::AttachEngine3D
  FirstAngle = 0
  Height = 8.5
  MapMode = 5
  Radius = 5.99
  SecondAngle = 0
  Support = -> [XY_Plane010]
FEATURE [PartDesign::AdditiveCone] Cone
  Angle = 360
  AttacherType = Attacher::AttachEngine3D
  BaseFeature = -> Cylinder002
  Height = 2
  MapMode = 5
  Radius1 = 7.1
  Radius2 = 5.1
  Support = -> [XY_Plane010]
FEATURE [PartDesign::AdditiveCone] Cone001
  Angle = 360
  AttacherType = Attacher::AttachEngine3D
  AttachmentOffset = pos=(0,0,-8.5) rot=(0,0,1;0rad)
  BaseFeature = -> Cone
  Height = 2
  MapMode = 5
  Placement = pos=(0,0,8.5) rot=(0,1,0;3.14159rad)
  Radius1 = 7.1
  Radius2 = 5.1
  Support = -> [XY_Plane010]
FEATURE [PartDesign::SubtractiveCylinder] Cylinder003
  Angle = 360
  AttacherType = Attacher::AttachEngine3D
  BaseFeature = -> Cone001
  FirstAngle = 0
  Height = 13
  MapMode = 5
  Radius = 4
  SecondAngle = 0
  Support = -> [XY_Plane010]
FEATURE [PartDesign::Body] Body006
  Group = -> [Cylinder002,Cone,Cone001,Cylinder003]
  Origin = -> Origin010
  Tip = -> Cylinder003
FEATURE [App::Part] Part003  label="Pully2GT20TSmooth"
  Group = -> [Body006]
  Origin = -> Origin009
---- part MGN9.FCStd = doc fcstd_087b5e8fa0dc ----
FCSTD DOCUMENT  (FreeCAD 0.20R29177 (Git))
Label: MGN9
License: All rights reserved
LicenseURL: http://en.wikipedia.org/wiki/All_rights_reserved
objects: PartDesign::Chamfer×7, PartDesign::Pad×6, PartDesign::Body×6, Sketcher::SketchObject×5, PartDesign::ShapeBinder×5, PartDesign::CoordinateSystem×4, App::DocumentObjectGroup×3, App::Part×3, PartDesign::Hole×2, App::Link×2, App::FeaturePython×1
note: 50 computed .brp shape members not serialized (recipe doc carries the construction recipe); baked Part::Feature solids carry a one-line shape summary decoded from their .brp

FEATURE [Sketcher::SketchObject] Sketch
  FullyConstrained = true
  MapMode = 5
  Placement = pos=(0,0,0) rot=(1,0,0;1.5708rad)
  Support = -> [XZ_Plane001]
  sketch-geometry (8):
    g0: LineSegment StartX=-4.5 StartY=6.5 StartZ=0 EndX=4.5 EndY=6.5 EndZ=0
    g1: LineSegment StartX=4.5 StartY=6.5 StartZ=0 EndX=4.5 EndY=5.5 EndZ=0
    g2: LineSegment StartX=4.5 StartY=0 StartZ=0 EndX=-4.5 EndY=0 EndZ=0
    g3: LineSegment StartX=-4.5 StartY=0 StartZ=0 EndX=-4.5 EndY=3.5 EndZ=0
    g4: ArcOfCircle CenterX=-4.5 CenterY=4.5 CenterZ=0 NormalX=0 NormalY=0 NormalZ=1 AngleXU=0 Radius=1 StartAngle=4.71239 EndAngle=7.85398
    g5: LineSegment StartX=-4.5 StartY=5.5 StartZ=0 EndX=-4.5 EndY=6.5 EndZ=0
    g6: ArcOfCircle CenterX=4.5 CenterY=4.5 CenterZ=0 NormalX=0 NormalY=0 NormalZ=1 AngleXU=0 Radius=1 StartAngle=1.5708 EndAngle=4.71239
    g7: LineSegment StartX=4.5 StartY=3.5 StartZ=0 EndX=4.5 EndY=0 EndZ=0
  constraints (22):
    c: Coincident(g0,g1)
    c: Coincident(g7,g2)
    c: Coincident(g2,g3)
    c: Coincident(g5,g0)
    c: Symmetric(g2,g7,g-2)
    c: Symmetric(g0,g0,g-2)
    c: Vertical(g3)
    c: DistanceX(g2,g2) = 9
    c: DistanceY(g3,g5) = 6.5
    c: PointOnObject(g2,g-1)
    c: PointOnObject(g4,g3)
    c: DistanceY(g-1,g4) = 4.5
    c: Radius(g4) = 1
    c: Coincident(g3,g4)
    c: Coincident(g5,g4)
    c: Vertical(g5)
    c: Vertical(g4,g3)
    c: PointOnObject(g6,g1)
    c: Coincident(g1,g6)
    c: Coincident(g7,g6)
    c: Symmetric(g4,g6,g-2)
    c: Symmetric(g3,g6,g-2)
FEATURE [Sketcher::SketchObject] Sketch001  label="UnitSketch"
  FullyConstrained = true
  MapMode = 5
  Placement = pos=(0,0,0) rot=(1,0,0;1.5708rad)
  Support = -> [XZ_Plane002]
  sketch-geometry (12):
    g0: LineSegment StartX=-10 StartY=8 StartZ=0 EndX=-4 EndY=8 EndZ=0
    g1: LineSegment StartX=10 StartY=8 StartZ=0 EndX=10 EndY=0 EndZ=0
    g2: LineSegment StartX=10 StartY=0 StartZ=0 EndX=4.5 EndY=0 EndZ=0
    g3: LineSegment StartX=-10 StartY=0 StartZ=0 EndX=-10 EndY=8 EndZ=0
    g4: LineSegment StartX=-4.5 StartY=4.5 StartZ=0 EndX=4.5 EndY=4.5 EndZ=0
    g5: LineSegment StartX=4.5 StartY=4.5 StartZ=0 EndX=4.5 EndY=0 EndZ=0
    g6: LineSegment StartX=-4.5 StartY=0 StartZ=0 EndX=-4.5 EndY=4.5 EndZ=0
    g7: LineSegment StartX=-4.5 StartY=0 StartZ=0 EndX=-10 EndY=0 EndZ=0
    g8: LineSegment StartX=4 StartY=8 StartZ=0 EndX=4 EndY=7.55 EndZ=0
    g9: LineSegment StartX=4 StartY=7.55 StartZ=0 EndX=-4 EndY=7.55 EndZ=0
    g10: LineSegment StartX=-4 StartY=7.55 StartZ=0 EndX=-4 EndY=8 EndZ=0
    g11: LineSegment StartX=4 StartY=8 StartZ=0 EndX=10 EndY=8 EndZ=0
  constraints (31):
    c: Coincident(g11,g1)
    c: Coincident(g1,g2)
    c: Coincident(g7,g3)
    c: Coincident(g3,g0)
    c: Symmetric(g7,g1,g-2)
    c: Symmetric(g0,g11,g-2)
    c: PointOnObject(g7,g-1)
    c: DistanceX(g7,g2) = 20
    c: DistanceY(g3,g3) = 8
    c: Vertical(g3)
    c: Coincident(g4,g5)
    c: Coincident(g6,g4)
    c: Horizontal(g4)
    c: Vertical(g5)
    c: Vertical(g6)
    c: Coincident(g2,g5)
    c: DistanceX(g6,g5) = 9
    c: DistanceY(g6,g6) = 4.5
    c: Symmetric(g6,g2,g-2)
    c: Coincident(g8,g9)
    c: Coincident(g9,g10)
    c: Coincident(g10,g0)
    c: Coincident(g8,g11)
    c: Symmetric(g0,g8,g-2)
    c: DistanceX(g9,g9) = 8
    c: Horizontal(g0)
    c: DistanceY(g10,g10) = 0.45
    c: Symmetric(g9,g8,g-2)
    c: Vertical(g10)
    c: Coincident(g7,g6)
    c: PointOnObject(g6,g-1)
FEATURE [Sketcher::SketchObject] Sketch002  label="CoverSketch"
  FullyConstrained = true
  MapMode = 5
  Placement = pos=(0,0,0) rot=(1,0,0;1.5708rad)
  Support = -> [XZ_Plane002]
  sketch-geometry (12):
    g0: LineSegment StartX=9.85 StartY=7.65 StartZ=0 EndX=9.85 EndY=0 EndZ=0
    g1: LineSegment StartX=9.85 StartY=0 StartZ=0 EndX=4.5 EndY=0 EndZ=0
    g2: LineSegment StartX=-9.85 StartY=0 StartZ=0 EndX=-9.85 EndY=7.65 EndZ=0
    g3: LineSegment StartX=-4.5 StartY=4.5 StartZ=0 EndX=4.5 EndY=4.5 EndZ=0
    g4: LineSegment StartX=4.5 StartY=4.5 StartZ=0 EndX=4.5 EndY=3.5 EndZ=0
    g5: LineSegment StartX=-4.5 StartY=0 StartZ=0 EndX=-4.5 EndY=1.5 EndZ=0
    g6: LineSegment StartX=-9.85 StartY=7.65 StartZ=0 EndX=9.85 EndY=7.65 EndZ=0
    g7: LineSegment StartX=-4.5 StartY=0 StartZ=0 EndX=-9.85 EndY=0 EndZ=0
    g8: ArcOfCircle CenterX=-4.5 CenterY=2.5 CenterZ=0 NormalX=0 NormalY=0 NormalZ=1 AngleXU=0 Radius=1 StartAngle=4.71239 EndAngle=7.85398
    g9: ArcOfCircle CenterX=4.5 CenterY=2.5 CenterZ=0 NormalX=0 NormalY=0 NormalZ=1 AngleXU=0 Radius=1 StartAngle=1.5708 EndAngle=4.71239
    g10: LineSegment StartX=-4.5 StartY=3.5 StartZ=0 EndX=-4.5 EndY=4.5 EndZ=0
    g11: LineSegment StartX=4.5 StartY=1.5 StartZ=0 EndX=4.5 EndY=0 EndZ=0
  constraints (32):
    c: Coincident(g6,g0)
    c: Coincident(g0,g1)
    c: Coincident(g7,g2)
    c: Vertical(g2)
    c: Coincident(g3,g4)
    c: Coincident(g10,g3)
    c: Vertical(g5)
    c: Coincident(g1,g11)
    c: Coincident(g5,g7)
    c: Symmetric(g2,g0,g-2)
    c: Symmetric(g5,g1,g-2)
    c: Symmetric(g3,g3,g-2)
    c: PointOnObject(g5,g-1)
    c: PointOnObject(g2,g-1)
    c: DistanceX(g3,g3) = 9
    c: DistanceY(g5,g10) = 4.5
    c: DistanceY(g2,g2) = 7.65
    c: Coincident(g6,g2)
    c: DistanceX(g6,g6) = 19.7
    c: Symmetric(g2,g0,g-2)
    c: PointOnObject(g8,g5)
    c: PointOnObject(g9,g4)
    c: Coincident(g5,g8)
    c: Coincident(g10,g8)
    c: Coincident(g4,g9)
    c: Coincident(g11,g9)
    c: Vertical(g8,g5)
    c: Vertical(g10)
    c: Symmetric(g8,g4,g-2)
    c: Symmetric(g9,g5,g-2)
    c: DistanceY(g5,g8) = 2.5
    c: Radius(g8) = 1
FEATURE [PartDesign::CoordinateSystem] LCS_Origin
  AttacherType = Attacher::AttachEngine3D
  MapMode = 2
  Support = -> [X_Axis008]
FEATURE [App::FeaturePython] Variables  # WARN: FeaturePython — macro-defined, semantics opaque (R4)
  Length = 100
  Position = 0
  Type = App::PropertyContainer
FEATURE [App::DocumentObjectGroup] Constraints
FEATURE [App::DocumentObjectGroup] Configurations
FEATURE [PartDesign::Pad] Pad
  Direction = (0,-1,-2e-16)
  Length = 100
  Length2 = 10
  Midplane = true
  Placement = pos=(0,0,0) rot=(1,0,0;1.5708rad)
  Profile = -> Sketch
  ReferenceAxis = -> Sketch [N_Axis]
  Type = 0
  expr: Length = <<Variables>>.Length
FEATURE [PartDesign::ShapeBinder] ShapeBinder
  Placement = pos=(0,0,0) rot=(1,0,0;1.5708rad)
  Support = -> [Sketch001]
  TraceSupport = false
FEATURE [PartDesign::Pad] Pad001
  Direction = (0,1,2e-16)
  Length = 18.9
  Length2 = 10
  Midplane = true
  Placement = pos=(0,0,0) rot=(1,0,0;1.5708rad)
  Profile = -> ShapeBinder
  Type = 0
FEATURE [PartDesign::ShapeBinder] ShapeBinder001
  Placement = pos=(0,0,0) rot=(1,0,0;1.5708rad)
  Support = -> [Sketch002]
  TraceSupport = false
FEATURE [PartDesign::Pad] Pad002
  Direction = (0,1,2e-16)
  Length = 4
  Length2 = 10
  Placement = pos=(0,0,0) rot=(1,0,0;1.5708rad)
  Profile = -> ShapeBinder001
  Type = 0
FEATURE [PartDesign::ShapeBinder] ShapeBinder002
  Placement = pos=(0,0,0) rot=(1,0,0;1.5708rad)
  Support = -> [Sketch002]
  TraceSupport = false
FEATURE [PartDesign::Pad] Pad003
  Direction = (0,1,2e-16)
  Length = 4
  Length2 = 10
  Placement = pos=(0,0,0) rot=(1,0,0;1.5708rad)
  Profile = -> ShapeBinder002
  Reversed = true
  Type = 0
FEATURE [PartDesign::Chamfer] Chamfer
  Angle = 45
  Base = -> Pad003 [Edge5,Edge8,Edge11,Edge2]
  BaseFeature = -> Pad003
  ChamferType = 0
  FlipDirection = false
  Placement = pos=(0,0,0) rot=(1,0,0;1.5708rad)
  Size = 1
  Size2 = 1
  SupportTransform = false
  UseAllEdges = false
FEATURE [PartDesign::Chamfer] Chamfer001
  Angle = 45
  Base = -> Pad001 [Edge5,Edge20,Edge23,Edge2]
  BaseFeature = -> Pad001
  ChamferType = 0
  FlipDirection = false
  Placement = pos=(0,0,0) rot=(1,0,0;1.5708rad)
  Size = 0.5
  Size2 = 1
  SupportTransform = false
  UseAllEdges = false
FEATURE [PartDesign::Chamfer] Chamfer002
  Angle = 45
  Base = -> Pad002 [Edge8,Edge5,Edge2,Edge11]
  BaseFeature = -> Pad002
  ChamferType = 0
  FlipDirection = false
  Placement = pos=(0,0,0) rot=(1,0,0;1.5708rad)
  Size = 1
  Size2 = 1
  SupportTransform = false
  UseAllEdges = false
FEATURE [PartDesign::Body] Body002  label="Returner001"
  Group = -> [ShapeBinder001,Pad002,Chamfer002]
  Origin = -> Origin004
  Placement = pos=(0,9.4,0) rot=(0,0,1;0rad)
  Tip = -> Chamfer002
FEATURE [PartDesign::Chamfer] Chamfer003
  Angle = 45
  Base = -> Pad [Edge2,Edge11,Edge14,Edge1]
  BaseFeature = -> Pad
  ChamferType = 0
  FlipDirection = false
  Placement = pos=(0,0,0) rot=(1,0,0;1.5708rad)
  Size = 0.35
  Size2 = 1
  SupportTransform = false
  UseAllEdges = false
FEATURE [PartDesign::ShapeBinder] ShapeBinder003
  Placement = pos=(0,0,0) rot=(1,0,0;1.5708rad)
  Support = -> [Sketch002]
  TraceSupport = false
FEATURE [PartDesign::Pad] Pad004
  Direction = (0,1,2e-16)
  Length = 1
  Length2 = 10
  Placement = pos=(0,0,0) rot=(1,0,0;1.5708rad)
  Profile = -> ShapeBinder003
  Type = 0
FEATURE [PartDesign::Chamfer] Chamfer004
  Angle = 45
  Base = -> Pad004 [Edge8,Edge5,Edge11,Edge2]
  BaseFeature = -> Pad004
  ChamferType = 0
  FlipDirection = false
  Placement = pos=(0,0,0) rot=(1,0,0;1.5708rad)
  Size = 1
  Size2 = 1
  SupportTransform = false
  UseAllEdges = false
FEATURE [PartDesign::Body] Body004  label="wiper001"
  Group = -> [ShapeBinder003,Pad004,Chamfer004]
  Origin = -> Origin006
  Placement = pos=(0,13.4,0) rot=(0,0,1;0rad)
  Tip = -> Chamfer004
FEATURE [PartDesign::ShapeBinder] ShapeBinder004
  Placement = pos=(0,0,0) rot=(1,0,0;1.5708rad)
  Support = -> [Sketch002]
  TraceSupport = false
FEATURE [PartDesign::Pad] Pad005
  Direction = (0,1,2e-16)
  Length = 1
  Length2 = 10
  Placement = pos=(0,0,0) rot=(1,0,0;1.5708rad)
  Profile = -> ShapeBinder004
  Reversed = true
  Type = 0
FEATURE [PartDesign::Chamfer] Chamfer005
  Angle = 45
  Base = -> Pad003 [Edge8,Edge11,Edge5,Edge2]
  BaseFeature = -> Pad003
  ChamferType = 0
  FlipDirection = false
  Placement = pos=(0,0,0) rot=(1,0,0;1.5708rad)
  Size = 1
  Size2 = 1
  SupportTransform = false
  UseAllEdges = false
FEATURE [PartDesign::Body] Body003  label="Returner002"
  Group = -> [ShapeBinder002,Pad003,Chamfer,Chamfer005]
  Origin = -> Origin005
  Placement = pos=(0,-9.4,0) rot=(0,0,1;0rad)
  Tip = -> Chamfer005
FEATURE [PartDesign::Chamfer] Chamfer006
  Angle = 45
  Base = -> Pad005 [Edge5,Edge2,Edge8,Edge11]
  BaseFeature = -> Pad005
  ChamferType = 0
  FlipDirection = false
  Placement = pos=(0,0,0) rot=(1,0,0;1.5708rad)
  Size = 1
  Size2 = 1
  SupportTransform = false
  UseAllEdges = false
FEATURE [PartDesign::Body] Body005  label="wiper002"
  Group = -> [ShapeBinder004,Pad005,Chamfer006]
  Origin = -> Origin007
  Placement = pos=(0,-13.4,0) rot=(0,0,1;0rad)
  Tip = -> Chamfer006
FEATURE [Sketcher::SketchObject] Sketch003
  FullyConstrained = true
  MapMode = 5
  Placement = pos=(0,1.8e-15,8) rot=(0,0,1;3.14159rad)
  Support = -> [Chamfer001]
  sketch-geometry (4):
    g0: Circle CenterX=-7.5 CenterY=5 CenterZ=0 NormalX=0 NormalY=0 NormalZ=1 AngleXU=0 Radius=1.5
    g1: Circle CenterX=7.5 CenterY=5 CenterZ=0 NormalX=0 NormalY=0 NormalZ=1 AngleXU=0 Radius=1.5
    g2: Circle CenterX=-7.5 CenterY=-5 CenterZ=0 NormalX=0 NormalY=0 NormalZ=1 AngleXU=0 Radius=1.5
    g3: Circle CenterX=7.5 CenterY=-5 CenterZ=0 NormalX=0 NormalY=0 NormalZ=1 AngleXU=0 Radius=1.5
  constraints (9):
    c: Symmetric(g0,g2,g-1)
    c: Symmetric(g0,g1,g-2)
    c: Symmetric(g2,g3,g-2)
    c: DistanceY(g2,g0) = 10
    c: DistanceX(g0,g1) = 15
    c: Equal(g0,g1)
    c: Equal(g0,g2)
    c: Equal(g0,g3)
    c: Diameter(g0) = 3
FEATURE [PartDesign::Hole] Hole
  BaseFeature = -> Chamfer001
  CustomThreadClearance = 0
  Depth = 4.4
  DepthType = 0
  Diameter = 2.5
  DrillForDepth = false
  DrillPoint = 1
  DrillPointAngle = 118
  HoleCutCountersinkAngle = 90
  HoleCutCustomValues = false
  HoleCutDepth = 0
  HoleCutDiameter = 6.1
  HoleCutType = 0
  ModelThread = false
  Placement = pos=(0,0,0) rot=(1,0,0;1.5708rad)
  Profile = -> Sketch003
  Tapered = false
  TaperedAngle = 90
  ThreadClass = 0
  ThreadDepth = 4.4
  ThreadDepthType = 0
  ThreadDirection = 0
  ThreadFit = 0
  ThreadSize = 9
  ThreadType = 1
  Threaded = true
  UseCustomThreadClearance = false
FEATURE [PartDesign::Body] Body001  label="UnitBody"
  Group = -> [ShapeBinder,Pad001,Chamfer001,Sketch003,Hole]
  Origin = -> Origin003
  Tip = -> Hole
FEATURE [PartDesign::CoordinateSystem] LCS_RailPartOrigin
  AttacherType = Attacher::AttachEngine3D
  MapMode = 3
  Placement = pos=(0,0,0) rot=(0,0,-1;1.5708rad)
  Support = -> [Y_Axis]
FEATURE [PartDesign::CoordinateSystem] LCS_RailPartTop
  AttacherType = Attacher::AttachEngine3D
  AttachmentOffset = pos=(0,0,6.5) rot=(0,0,1;0rad)
  MapMode = 3
  Placement = pos=(-7e-16,7e-16,6.5) rot=(0,0,-1;1.5708rad)
  Support = -> [Y_Axis]
FEATURE [PartDesign::CoordinateSystem] LCS_UnitPartOrigin
  AttacherType = Attacher::AttachEngine3D
  AttachmentOffset = pos=(0,0,4.5) rot=(0,0,1;0rad)
  MapMode = 3
  Placement = pos=(-5e-16,5e-16,4.5) rot=(0,0,-1;1.5708rad)
  Support = -> [Y_Axis002]
FEATURE [App::Part] Part001  label="Unit"
  Group = -> [Sketch001,Sketch002,Body001,Body002,Body003,Body004,Body005,LCS_UnitPartOrigin]
  Origin = -> Origin002
FEATURE [App::Link] Rail  label="Rail001"
  AssemblyType = Part::Link
  AttachedBy = #LCS_RailPartOrigin
  AttachedTo = Parent Assembly#LCS_Origin
  LinkPlacement = pos=(0,0,0) rot=(0,0,1;1.5708rad)
  LinkedObject = -> Part
  Placement = pos=(0,0,0) rot=(0,0,1;1.5708rad)
  SolverId = Asm4EE
  expr: Placement = LCS_Origin.Placement * AttachmentOffset * LCS_RailPartOrigin.Placement ^ -1
FEATURE [App::Link] Unit  label="Unit001"
  AssemblyType = Part::Link
  AttachedBy = #LCS_UnitPartOrigin
  AttachedTo = Rail#LCS_RailPartTop
  LinkPlacement = pos=(0,0,2) rot=(0,0,1;1.5708rad)
  LinkedObject = -> Part001
  Placement = pos=(0,0,2) rot=(0,0,1;1.5708rad)
  SolverId = Asm4EE
  expr: .AttachmentOffset.Base.x = <<Variables>>.Position
  expr: Placement = Rail.Placement * LCS_RailPartTop.Placement * AttachmentOffset * LCS_UnitPartOrigin.Placement ^ -1
FEATURE [App::Part] Assembly
  AssemblyType = Part::Link
  Group = -> [LCS_Origin,Variables,Constraints,Configurations,Rail,Unit]
  Origin = -> Origin008
  Type = Assembly
FEATURE [Sketcher::SketchObject] Sketch004
  AttachmentOffset = pos=(0,0,-6.5) rot=(0,0,1;0rad)
  FullyConstrained = true
  MapMode = 3
  Placement = pos=(-7e-16,7e-16,6.5) rot=(0.707107,0.707107,0;3.14159rad)
  Support = -> [Y_Axis001]
  sketch-geometry (19):
    g0: Circle CenterX=0 CenterY=0 CenterZ=0 NormalX=0 NormalY=0 NormalZ=1 AngleXU=0 Radius=1.5
    g1: Circle CenterX=-20 CenterY=0 CenterZ=0 NormalX=0 NormalY=0 NormalZ=1 AngleXU=0 Radius=1.5
    g2: Circle CenterX=-40 CenterY=0 CenterZ=0 NormalX=0 NormalY=0 NormalZ=1 AngleXU=0 Radius=1.5
    g3: Circle CenterX=-60 CenterY=0 CenterZ=0 NormalX=0 NormalY=0 NormalZ=1 AngleXU=0 Radius=1.5
    g4: Circle CenterX=-80 CenterY=0 CenterZ=0 NormalX=0 NormalY=0 NormalZ=1 AngleXU=0 Radius=1.5
    g5: Circle CenterX=-100 CenterY=0 CenterZ=0 NormalX=0 NormalY=0 NormalZ=1 AngleXU=0 Radius=1.5
    g6: Circle CenterX=-120 CenterY=0 CenterZ=0 NormalX=0 NormalY=0 NormalZ=1 AngleXU=0 Radius=1.5
    g7: Circle CenterX=-140 CenterY=0 CenterZ=0 NormalX=0 NormalY=0 NormalZ=1 AngleXU=0 Radius=1.5
    g8: Circle CenterX=-160 CenterY=0 CenterZ=0 NormalX=0 NormalY=0 NormalZ=1 AngleXU=0 Radius=1.5
    g9: Circle CenterX=-180 CenterY=0 CenterZ=0 NormalX=0 NormalY=0 NormalZ=1 AngleXU=0 Radius=1.5
    g10: Circle CenterX=20 CenterY=0 CenterZ=0 NormalX=0 NormalY=0 NormalZ=1 AngleXU=0 Radius=1.5
    g11: Circle CenterX=40 CenterY=0 CenterZ=0 NormalX=0 NormalY=0 NormalZ=1 AngleXU=0 Radius=1.5
    g12: Circle CenterX=60 CenterY=0 CenterZ=0 NormalX=0 NormalY=0 NormalZ=1 AngleXU=0 Radius=1.5
    g13: Circle CenterX=80 CenterY=0 CenterZ=0 NormalX=0 NormalY=0 NormalZ=1 AngleXU=0 Radius=1.5
    g14: Circle CenterX=100 CenterY=0 CenterZ=0 NormalX=0 NormalY=0 NormalZ=1 AngleXU=0 Radius=1.5
    g15: Circle CenterX=120 CenterY=0 CenterZ=0 NormalX=0 NormalY=0 NormalZ=1 AngleXU=0 Radius=1.5
    g16: Circle CenterX=140 CenterY=0 CenterZ=0 NormalX=0 NormalY=0 NormalZ=1 AngleXU=0 Radius=1.5
    g17: Circle CenterX=160 CenterY=0 CenterZ=0 NormalX=0 NormalY=0 NormalZ=1 AngleXU=0 Radius=1.5
    g18: Circle CenterX=180 CenterY=0 CenterZ=0 NormalX=0 NormalY=0 NormalZ=1 AngleXU=0 Radius=1.5
  constraints (30):
    c: PointOnObject(g1,g-1)
    c: PointOnObject(g2,g-1)
    c: PointOnObject(g3,g-1)
    c: PointOnObject(g4,g-1)
    c: PointOnObject(g5,g-1)
    c: PointOnObject(g6,g-1)
    c: PointOnObject(g7,g-1)
    c: PointOnObject(g8,g-1)
    c: PointOnObject(g9,g-1)
    c: Equal(g0, g1-g18) x18
    c: Diameter(g0) = 3
    c: Symmetric(g9,g18,g-2)
    c: Symmetric(g8,g17,g-2)
    c: DistanceX(g9,g8) = 20
    c: Symmetric(g7,g16,g-2)
    c: DistanceX(g8,g7) = 20
    c: Symmetric(g6,g15,g-2)
    c: DistanceX(g7,g6) = 20
    c: Symmetric(g14,g5,g-2)
    c: DistanceX(g6,g5) = 20
    c: Symmetric(g4,g13,g-2)
    c: DistanceX(g5,g4) = 20
    c: Symmetric(g12,g3,g-2)
    c: DistanceX(g4,g3) = 20
    c: Symmetric(g11,g2,g-2)
    c: DistanceX(g3,g2) = 20
    c: Symmetric(g10,g1,g-2)
    c: DistanceX(g2,g1) = 20
    c: DistanceX(g1,g0) = 20
    c: Coincident(g0,g-1)
FEATURE [PartDesign::Hole] Hole001
  BaseFeature = -> Chamfer003
  CustomThreadClearance = 0
  Depth = 733.603
  DepthType = 1
  Diameter = 3.7
  DrillForDepth = false
  DrillPoint = 1
  DrillPointAngle = 118
  HoleCutCountersinkAngle = 90
  HoleCutCustomValues = false
  HoleCutDepth = 3.06
  HoleCutDiameter = 6.1
  HoleCutType = 1
  ModelThread = false
  Placement = pos=(0,0,0) rot=(1,0,0;1.5708rad)
  Profile = -> Sketch004
  Reversed = true
  Tapered = false
  TaperedAngle = 90
  ThreadClass = 0
  ThreadDepth = 733.603
  ThreadDepthType = 0
  ThreadDirection = 0
  ThreadFit = 0
  ThreadSize = 0
  ThreadType = 0
  Threaded = false
  UseCustomThreadClearance = false
FEATURE [PartDesign::Body] Body  label="RailBody"
  Group = -> [Sketch,Pad,Sketch004,Chamfer003,Hole001]
  Origin = -> Origin001
  Tip = -> Hole001
FEATURE [App::Part] Part  label="Rail"
  Group = -> [Body,LCS_RailPartOrigin,LCS_RailPartTop]
  Origin = -> Origin
FEATURE [App::DocumentObjectGroup] Parts
  Group = -> [Part,Part001]
---- part miniXY-Frame.FCStd = doc fcstd_6a076cb3e2fe (504191 chars; too large to inline — full recipe in that document) ----
---- part miniXY-PrintBed.FCStd = doc fcstd_e5c5c3b6efab ----
FCSTD DOCUMENT  (FreeCAD 0.20R29177 (Git))
Label: miniXY-PrintBed
License: All rights reserved
LicenseURL: http://en.wikipedia.org/wiki/All_rights_reserved
objects: Sketcher::SketchObject×7, PartDesign::Pad×7, PartDesign::Body×7, PartDesign::CoordinateSystem×3, App::DocumentObjectGroup×3, App::Part×3, App::Link×2, App::FeaturePython×1
note: 31 computed .brp shape members not serialized (recipe doc carries the construction recipe); baked Part::Feature solids carry a one-line shape summary decoded from their .brp

FEATURE [PartDesign::CoordinateSystem] LCS_Origin
  AttacherType = Attacher::AttachEngine3D
  MapMode = 2
  Support = -> [X_Axis]
FEATURE [App::DocumentObjectGroup] Constraints
FEATURE [App::FeaturePython] Variables  # WARN: FeaturePython — macro-defined, semantics opaque (R4)
  BedSize = 150
  BedThickness = 7
  GantorySpacing = 200
  Type = App::PropertyContainer
FEATURE [App::DocumentObjectGroup] Configurations
FEATURE [Sketcher::SketchObject] Sketch
  FullyConstrained = true
  MapMode = 5
  Support = -> [XY_Plane002]
  expr: Constraints[10] = <<Variables>>.BedSize
  sketch-geometry (4):
    g0: LineSegment StartX=-75 StartY=75 StartZ=0 EndX=75 EndY=75 EndZ=0
    g1: LineSegment StartX=75 StartY=75 StartZ=0 EndX=75 EndY=-75 EndZ=0
    g2: LineSegment StartX=75 StartY=-75 StartZ=0 EndX=-75 EndY=-75 EndZ=0
    g3: LineSegment StartX=-75 StartY=-75 StartZ=0 EndX=-75 EndY=75 EndZ=0
  constraints (11):
    c: Coincident(g0,g1)
    c: Coincident(g1,g2)
    c: Coincident(g2,g3)
    c: Coincident(g3,g0)
    c: Horizontal(g0)
    c: Horizontal(g2)
    c: Vertical(g1)
    c: Vertical(g3)
    c: Symmetric(g0,g1,g-1)
    c: Equal(g0,g3)
    c: Distance(g3) = 150
FEATURE [PartDesign::Pad] Pad
  Direction = (0,0,1)
  Length = 7
  Length2 = 10
  Profile = -> Sketch
  ReferenceAxis = -> Sketch [N_Axis]
  Type = 0
  expr: Length = <<Variables>>.BedThickness
FEATURE [PartDesign::Body] Body  label="Bed"
  Group = -> [Sketch,Pad]
  Origin = -> Origin002
  Tip = -> Pad
FEATURE [Sketcher::SketchObject] Sketch001
  AttachmentOffset = pos=(0,0,7) rot=(0,0,1;0rad)
  FullyConstrained = false
  MapMode = 5
  Placement = pos=(0,0,7) rot=(0,0,1;0rad)
  Support = -> [XY_Plane003]
  expr: .AttachmentOffset.Base.z = <<Variables>>.BedThickness
  expr: Constraints[12] = <<Variables>>.BedSize / 2 - 15
  expr: Constraints[9] = <<Variables>>.BedSize
  sketch-geometry (5):
    g0: LineSegment StartX=-75 StartY=58.3105 StartZ=0 EndX=75 EndY=58.3105 EndZ=0
    g1: LineSegment StartX=75 StartY=58.3105 StartZ=0 EndX=75 EndY=-58.3105 EndZ=0
    g2: LineSegment StartX=75 StartY=-58.3105 StartZ=0 EndX=-75 EndY=-58.3105 EndZ=0
    g3: LineSegment StartX=-75 StartY=-58.3105 StartZ=0 EndX=-75 EndY=91.6895 EndZ=0
    g4: Circle CenterX=0 CenterY=60 CenterZ=0 NormalX=0 NormalY=0 NormalZ=1 AngleXU=0 Radius=6
  constraints (13):
    c: Coincident(g0,g1)
    c: Coincident(g1,g2)
    c: Coincident(g2,g3)
    c: Horizontal(g0)
    c: Horizontal(g2)
    c: Vertical(g1)
    c: Vertical(g3)
    c: Symmetric(g0,g1,g-1)
    c: Equal(g0,g3)
    c: Distance(g3) = 150
    c: PointOnObject(g4,g-2)
    c: Diameter(g4) = 12
    c: DistanceY(g4) = 60
FEATURE [Sketcher::SketchObject] Sketch002
  AttachmentOffset = pos=(0,0,7) rot=(0,0,1;0rad)
  FullyConstrained = true
  MapMode = 5
  Placement = pos=(0,0,7) rot=(0,0,1;0rad)
  Support = -> [XY_Plane004]
  expr: .AttachmentOffset.Base.z = <<Variables>>.BedThickness
  expr: Constraints[10] = <<Variables>>.BedSize
  expr: Constraints[11] = -(<<Variables>>.BedSize / 2 - 15)
  expr: Constraints[12] = -(<<Variables>>.BedSize / 2 - 15)
  sketch-geometry (5):
    g0: LineSegment StartX=-75 StartY=75 StartZ=0 EndX=75 EndY=75 EndZ=0
    g1: LineSegment StartX=75 StartY=75 StartZ=0 EndX=75 EndY=-75 EndZ=0
    g2: LineSegment StartX=75 StartY=-75 StartZ=0 EndX=-75 EndY=-75 EndZ=0
    g3: LineSegment StartX=-75 StartY=-75 StartZ=0 EndX=-75 EndY=75 EndZ=0
    g4: Circle CenterX=-60 CenterY=-60 CenterZ=0 NormalX=0 NormalY=0 NormalZ=1 AngleXU=0 Radius=6
  constraints (14):
    c: Coincident(g0,g1)
    c: Coincident(g1,g2)
    c: Coincident(g2,g3)
    c: Coincident(g3,g0)
    c: Horizontal(g0)
    c: Horizontal(g2)
    c: Vertical(g1)
    c: Vertical(g3)
    c: Symmetric(g1,g0,g-1)
    c: Equal(g0,g3)
    c: Distance(g3) = 150
    c: DistanceY(g4) = -60
    c: DistanceX(g4) = -60
    c: Diameter(g4) = 12
FEATURE [Sketcher::SketchObject] Sketch003
  AttachmentOffset = pos=(0,0,7) rot=(0,0,1;0rad)
  FullyConstrained = true
  MapMode = 5
  Placement = pos=(0,0,7) rot=(0,0,1;0rad)
  Support = -> [XY_Plane005]
  expr: .AttachmentOffset.Base.z = <<Variables>>.BedThickness
  expr: Constraints[10] = <<Variables>>.BedSize
  expr: Constraints[11] = <<Variables>>.BedSize / 2 - 15
  expr: Constraints[12] = -(<<Variables>>.BedSize / 2 - 15)
  sketch-geometry (5):
    g0: LineSegment StartX=-75 StartY=75 StartZ=0 EndX=75 EndY=75 EndZ=0
    g1: LineSegment StartX=75 StartY=75 StartZ=0 EndX=75 EndY=-75 EndZ=0
    g2: LineSegment StartX=75 StartY=-75 StartZ=0 EndX=-75 EndY=-75 EndZ=0
    g3: LineSegment StartX=-75 StartY=-75 StartZ=0 EndX=-75 EndY=75 EndZ=0
    g4: Circle CenterX=60 CenterY=-60 CenterZ=0 NormalX=0 NormalY=0 NormalZ=1 AngleXU=0 Radius=6
  constraints (14):
    c: Coincident(g0,g1)
    c: Coincident(g1,g2)
    c: Coincident(g2,g3)
    c: Coincident(g3,g0)
    c: Horizontal(g0)
    c: Horizontal(g2)
    c: Vertical(g1)
    c: Vertical(g3)
    c: Symmetric(g0,g1,g-1)
    c: Equal(g0,g3)
    c: Distance(g3) = 150
    c: DistanceX(g4) = 60
    c: DistanceY(g4) = -60
    c: Diameter(g4) = 12
FEATURE [PartDesign::Pad] Pad001
  Direction = (0,0,1)
  Length = 10
  Length2 = 10
  Profile = -> Sketch001
  ReferenceAxis = -> Sketch001 [N_Axis]
  Type = 0
FEATURE [PartDesign::Body] Body001  label="BootRear"
  Group = -> [Sketch001,Pad001]
  Origin = -> Origin003
  Tip = -> Pad001
FEATURE [PartDesign::Pad] Pad002
  Direction = (0,0,1)
  Length = 10
  Length2 = 10
  Profile = -> Sketch002
  ReferenceAxis = -> Sketch002 [N_Axis]
  Type = 0
FEATURE [PartDesign::Body] Body002  label="BootFrontLeft"
  Group = -> [Sketch002,Pad002]
  Origin = -> Origin004
  Tip = -> Pad002
FEATURE [PartDesign::Pad] Pad003
  Direction = (0,0,1)
  Length = 10
  Length2 = 10
  Profile = -> Sketch003
  ReferenceAxis = -> Sketch003 [N_Axis]
  Type = 0
FEATURE [PartDesign::Body] Body003  label="BootFrontRight"
  Group = -> [Sketch003,Pad003]
  Origin = -> Origin005
  Tip = -> Pad003
FEATURE [Sketcher::SketchObject] Sketch004
  FullyConstrained = true
  MapMode = 5
  Placement = pos=(0,0,0) rot=(0.57735,0.57735,0.57735;2.0944rad)
  Support = -> [YZ_Plane006]
  expr: Constraints[11] = -(<<Variables>>.BedSize / 2 - 15)
  expr: Constraints[12] = 10 + <<Variables>>.BedThickness
  sketch-geometry (5):
    g0: LineSegment StartX=-65 StartY=27 StartZ=0 EndX=-55 EndY=27 EndZ=0
    g1: LineSegment StartX=-55 StartY=27 StartZ=0 EndX=-55 EndY=17 EndZ=0
    g2: LineSegment StartX=-55 StartY=17 StartZ=0 EndX=-65 EndY=17 EndZ=0
    g3: LineSegment StartX=-65 StartY=17 StartZ=0 EndX=-65 EndY=27 EndZ=0
    g4: GeomPoint X=-60 Y=22 Z=0
  constraints (13):
    c: Coincident(g0,g1)
    c: Coincident(g1,g2)
    c: Coincident(g2,g3)
    c: Coincident(g3,g0)
    c: Horizontal(g0)
    c: Horizontal(g2)
    c: Vertical(g1)
    c: Vertical(g3)
    c: Equal(g0,g3)
    c: Distance(g3) = 10
    c: Symmetric(g0,g1,g4)
    c: DistanceX(g4) = -60
    c: DistanceY(g2) = 17
FEATURE [PartDesign::Pad] Pad004
  Direction = (1,-2e-16,3e-16)
  Length = 200
  Length2 = 10
  Midplane = true
  Placement = pos=(0,0,0) rot=(0.57735,0.57735,0.57735;2.0944rad)
  Profile = -> Sketch004
  ReferenceAxis = -> Sketch004 [N_Axis]
  Type = 0
  expr: Length = Variables.GantorySpacing
FEATURE [PartDesign::Body] Body004  label="FrameFront"
  Group = -> [Sketch004,Pad004]
  Origin = -> Origin006
  Tip = -> Pad004
FEATURE [Sketcher::SketchObject] Sketch005
  FullyConstrained = true
  MapMode = 5
  Placement = pos=(0,0,0) rot=(0.57735,0.57735,0.57735;2.0944rad)
  Support = -> [YZ_Plane007]
  expr: Constraints[11] = <<Variables>>.BedSize / 2 - 15
  expr: Constraints[12] = 10 + <<Variables>>.BedThickness
  sketch-geometry (5):
    g0: LineSegment StartX=55 StartY=27 StartZ=0 EndX=65 EndY=27 EndZ=0
    g1: LineSegment StartX=65 StartY=27 StartZ=0 EndX=65 EndY=17 EndZ=0
    g2: LineSegment StartX=65 StartY=17 StartZ=0 EndX=55 EndY=17 EndZ=0
    g3: LineSegment StartX=55 StartY=17 StartZ=0 EndX=55 EndY=27 EndZ=0
    g4: GeomPoint X=60 Y=22 Z=0
  constraints (13):
    c: Coincident(g0,g1)
    c: Coincident(g1,g2)
    c: Coincident(g2,g3)
    c: Coincident(g3,g0)
    c: Horizontal(g0)
    c: Horizontal(g2)
    c: Vertical(g1)
    c: Vertical(g3)
    c: Symmetric(g0,g1,g4)
    c: Equal(g0,g3)
    c: Distance(g3) = 10
    c: DistanceX(g4) = 60
    c: DistanceY(g2) = 17
FEATURE [PartDesign::Pad] Pad005
  Direction = (1,-2e-16,3e-16)
  Length = 200
  Length2 = 10
  Midplane = true
  Placement = pos=(0,0,0) rot=(0.57735,0.57735,0.57735;2.0944rad)
  Profile = -> Sketch005
  ReferenceAxis = -> Sketch005 [N_Axis]
  Type = 0
  expr: Length = <<Variables>>.GantorySpacing
FEATURE [PartDesign::Body] Body005  label="FrameRear"
  Group = -> [Sketch005,Pad005]
  Origin = -> Origin007
  Tip = -> Pad005
FEATURE [Sketcher::SketchObject] Sketch006
  AttachmentOffset = pos=(0,0,100) rot=(0,0,1;0rad)
  FullyConstrained = true
  MapMode = 5
  Placement = pos=(100,-2.22e-14,2.22e-14) rot=(0.57735,0.57735,0.57735;2.0944rad)
  Support = -> [YZ_Plane008]
  expr: .AttachmentOffset.Base.z = Variables.GantorySpacing / 2
  sketch-geometry (20):
    g0: LineSegment StartX=10 StartY=12.5 StartZ=0 EndX=10 EndY=-12.5 EndZ=0
    g1: LineSegment StartX=-10 StartY=-12.5 StartZ=0 EndX=-10 EndY=12.5 EndZ=0
    g2: ArcOfCircle CenterX=-7.5 CenterY=12.5 CenterZ=0 NormalX=0 NormalY=0 NormalZ=1 AngleXU=0 Radius=2.5 StartAngle=1.5708 EndAngle=3.14159
    g3: GeomPoint X=-10 Y=15 Z=0
    g4: ArcOfCircle CenterX=-7.5 CenterY=-12.5 CenterZ=0 NormalX=0 NormalY=0 NormalZ=1 AngleXU=0 Radius=2.5 StartAngle=3.14159 EndAngle=4.71239
    g5: GeomPoint X=-10 Y=-15 Z=0
    g6: ArcOfCircle CenterX=7.5 CenterY=-12.5 CenterZ=0 NormalX=0 NormalY=0 NormalZ=1 AngleXU=0 Radius=2.5 StartAngle=4.71239 EndAngle=6.28319
    g7: GeomPoint X=10 Y=-15 Z=0
    g8: ArcOfCircle CenterX=7.5 CenterY=12.5 CenterZ=0 NormalX=0 NormalY=0 NormalZ=1 AngleXU=0 Radius=2.5 StartAngle=0 EndAngle=1.5708
    g9: GeomPoint X=10 Y=15 Z=0
    g10: ArcOfCircle CenterX=0 CenterY=12.5 CenterZ=0 NormalX=0 NormalY=0 NormalZ=1 AngleXU=0 Radius=6 StartAngle=0.562536 EndAngle=2.57906
    g11: ArcOfCircle CenterX=-6.34429 CenterY=16.5 CenterZ=0 NormalX=0 NormalY=0 NormalZ=1 AngleXU=0 Radius=1.5 StartAngle=4.71239 EndAngle=5.72065
    g12: ArcOfCircle CenterX=6.34429 CenterY=16.5 CenterZ=0 NormalX=0 NormalY=0 NormalZ=1 AngleXU=0 Radius=1.5 StartAngle=3.70413 EndAngle=4.71239
    g13: ArcOfCircle CenterX=0 CenterY=-12.5 CenterZ=0 NormalX=0 NormalY=0 NormalZ=1 AngleXU=0 Radius=6 StartAngle=3.70413 EndAngle=5.72065
    g14: ArcOfCircle CenterX=-6.34429 CenterY=-16.5 CenterZ=0 NormalX=0 NormalY=0 NormalZ=1 AngleXU=0 Radius=1.5 StartAngle=0.562536 EndAngle=1.5708
    g15: ArcOfCircle CenterX=6.34429 CenterY=-16.5 CenterZ=0 NormalX=0 NormalY=0 NormalZ=1 AngleXU=0 Radius=1.5 StartAngle=1.5708 EndAngle=2.57906
    g16: LineSegment StartX=-7.5 StartY=15 StartZ=0 EndX=-6.34429 EndY=15 EndZ=0
    g17: LineSegment StartX=6.34429 StartY=15 StartZ=0 EndX=7.5 EndY=15 EndZ=0
    g18: LineSegment StartX=-6.34429 StartY=-15 StartZ=0 EndX=-7.5 EndY=-15 EndZ=0
    g19: LineSegment StartX=7.5 StartY=-15 StartZ=0 EndX=6.34429 EndY=-15 EndZ=0
  constraints (46):
    c: Vertical(g0)
    c: Vertical(g1)
    c: Symmetric(g3,g7,g-1)
    c: PointOnObject(g3,g1)
    c: Tangent(g16,g2) = 1.5708
    c: Tangent(g1,g2) = 1.5708
    c: PointOnObject(g5,g1)
    c: Tangent(g1,g4) = 1.5708
    c: Tangent(g18,g4) = 1.5708
    c: PointOnObject(g7,g0)
    c: Tangent(g19,g6) = 1.5708
    c: Tangent(g0,g6) = 1.5708
    c: PointOnObject(g9,g0)
    c: Tangent(g0,g8) = 1.5708
    c: Tangent(g17,g8) = 1.5708
    c: Equal(g2,g4)
    c: Radius(g2) = 2.5
    c: Tangent(g10,g11) = 1.5708
    c: Tangent(g10,g12) = 1.5708
    c: PointOnObject(g10,g-2)
    c: Horizontal(g16)
    c: PointOnObject(g3,g16)
    c: Horizontal(g17)
    c: PointOnObject(g9,g17)
    c: Tangent(g11,g16) = -1.5708
    c: Tangent(g12,g17) = -1.5708
    c: Diameter(g10) = 12
    c: Equal(g11,g12)
    c: Diameter(g11) = 3
    c: Tangent(g14,g13) = 1.5708
    c: Tangent(g13,g15) = 1.5708
    c: Horizontal(g18)
    c: PointOnObject(g5,g18)
    c: Horizontal(g19)
    c: PointOnObject(g7,g19)
    c: Tangent(g14,g18) = -1.5708
    c: Symmetric(g13,g10,g-1)
    c: Tangent(g15,g19) = -1.5708
    c: Equal(g14,g11)
    c: Equal(g15,g11)
    c: Equal(g13,g10)
    c: DistanceY(g5,g3) = 30
    c: DistanceX(g3,g9) = 20
    c: Symmetric(g2,g8,g-2)
    c: Symmetric(g6,g4,g-2)
    c: DistanceY(g13,g10) = 25
FEATURE [PartDesign::Pad] Pad006
  Direction = (1,-2e-16,3e-16)
  Length = 10
  Length2 = 10
  Placement = pos=(0,0,0) rot=(0.57735,0.57735,0.57735;2.0944rad)
  Profile = -> Sketch006
  ReferenceAxis = -> Sketch006 [N_Axis]
  Reversed = true
  Type = 0
FEATURE [PartDesign::Body] Body006  label="CarriageLeftBase"
  Group = -> [Sketch006,Pad006]
  Origin = -> Origin008
  Tip = -> Pad006
FEATURE [PartDesign::CoordinateSystem] LCS_PrintBedOrigin
  AttacherType = Attacher::AttachEngine3D
  AttachmentOffset = pos=(0,0,-22) rot=(0,0,-1;1.5708rad)
  MapMode = 3
  Placement = pos=(-2.4e-15,2.4e-15,22) rot=(0,1,0;3.14159rad)
  Support = -> [Y_Axis001]
FEATURE [App::Part] Part  label="PrintBed"
  Group = -> [Body,Body001,Body002,Body003,Body004,Body005,LCS_PrintBedOrigin]
  Origin = -> Origin001
FEATURE [App::Link] PrintBed  label="PrintBed001"
  AssemblyType = Part::Link
  AttachedBy = #LCS_PrintBedOrigin
  AttachedTo = Parent Assembly#LCS_Origin
  LinkPlacement = pos=(1e-16,0,22) rot=(0,-1,0;3.14159rad)
  LinkedObject = -> Part
  Placement = pos=(1e-16,0,22) rot=(0,-1,0;3.14159rad)
  SolverId = Asm4EE
  expr: Placement = LCS_Origin.Placement * AttachmentOffset * LCS_PrintBedOrigin.Placement ^ -1
FEATURE [App::Link] CarriageLeft  label="CarriageLeft001"
  AttachedBy = #LCS_CarriageLeftOrigin
  AttachedTo = Parent Assembly#LCS_Origin
  LinkPlacement = pos=(0,0,0) rot=(0,-1,0;3.14159rad)
  LinkedObject = -> Part001
  Placement = pos=(0,0,0) rot=(0,-1,0;3.14159rad)
  SolverId = Asm4EE
  expr: Placement = LCS_Origin.Placement * AttachmentOffset * LCS_CarriageLeftOrigin.Placement ^ -1
FEATURE [App::Part] Model
  Group = -> [LCS_Origin,Constraints,Variables,Configurations,PrintBed,CarriageLeft]
  Origin = -> Origin
  Type = Assembly
FEATURE [PartDesign::CoordinateSystem] LCS_CarriageLeftOrigin
  AttacherType = Attacher::AttachEngine3D
  AttachmentOffset = pos=(0,0,0) rot=(0,0,-1;1.5708rad)
  MapMode = 3
  Placement = pos=(0,0,0) rot=(0,1,0;3.14159rad)
  Support = -> [Y_Axis009]
FEATURE [App::Part] Part001  label="CarriageLeft"
  Group = -> [Body006,LCS_CarriageLeftOrigin]
  Origin = -> Origin009
FEATURE [App::DocumentObjectGroup] Parts
  Group = -> [Part,Part001]
---- part miniXY-XYCarriage.FCStd = doc fcstd_459d2d5a2655 ----
FCSTD DOCUMENT  (FreeCAD 0.20R29177 (Git))
Label: miniXY-XYCarriage
License: All rights reserved
LicenseURL: http://en.wikipedia.org/wiki/All_rights_reserved
objects: PartDesign::CoordinateSystem×10, Sketcher::SketchObject×10, PartDesign::Body×9, PartDesign::Pad×7, PartDesign::Boolean×7, App::Part×5, PartDesign::AdditivePrism×4, PartDesign::ShapeBinder×4, App::DocumentObjectGroup×3, App::Link×3, PartDesign::Hole×2, Part::FeaturePython×2, App::FeaturePython×1, PartDesign::AdditiveLoft×1
note: 70 computed .brp shape members not serialized (recipe doc carries the construction recipe); baked Part::Feature solids carry a one-line shape summary decoded from their .brp

FEATURE [PartDesign::Body] Body001  label="CarriageBaseBrace"
  Origin = -> Origin002
FEATURE [PartDesign::Body] Body003  label="CarriageLeftBrace"
  Origin = -> Origin005
FEATURE [PartDesign::CoordinateSystem] LCS_Origin
  AttacherType = Attacher::AttachEngine3D
  MapMode = 2
  Support = -> [X_Axis006]
FEATURE [App::DocumentObjectGroup] Constraints
FEATURE [App::FeaturePython] Variables  # WARN: FeaturePython — macro-defined, semantics opaque (R4)
  CarriageThickness = 7
  GantorySpacing = 200
  IdlerDiameter = 12.73
  IdlerHeight = 8.5
  Type = App::PropertyContainer
  WasherThickness = 0.5
FEATURE [App::DocumentObjectGroup] Configurations
FEATURE [PartDesign::CoordinateSystem] LCS_CarriageLeftPosition
  AttacherType = Attacher::AttachEngine3D
  AttachmentOffset = pos=(-100,0,0) rot=(0,0,1;0rad)
  MapMode = 2
  Placement = pos=(-100,0,0) rot=(0,0,1;0rad)
  Support = -> [X_Axis014]
  expr: .AttachmentOffset.Base.x = -<<Variables>>.GantorySpacing / 2
FEATURE [PartDesign::CoordinateSystem] LCS_CarriageRightPosition
  AttacherType = Attacher::AttachEngine3D
  AttachmentOffset = pos=(100,0,0) rot=(0,0,1;0rad)
  MapMode = 2
  Placement = pos=(100,0,0) rot=(0,0,1;0rad)
  Support = -> [X_Axis014]
  expr: .AttachmentOffset.Base.x = <<Variables>>.GantorySpacing / 2
FEATURE [Sketcher::SketchObject] Sketch
  AttachmentOffset = pos=(0,0,6) rot=(0,0,1;0rad)
  FullyConstrained = true
  MapMode = 5
  Placement = pos=(0,0,6) rot=(0,0,1;0rad)
  Support = -> [XY_Plane001]
  expr: .AttachmentOffset.Base.z = <<Variables>>.CarriageThickness - 1
  sketch-geometry (18):
    g0: LineSegment StartX=-16 StartY=-7.5 StartZ=0 EndX=-16 EndY=7.5 EndZ=0
    g1: LineSegment StartX=16 StartY=7.5 StartZ=0 EndX=16 EndY=-7.5 EndZ=0
    g2: LineSegment StartX=13.5 StartY=-10 StartZ=0 EndX=-13.5 EndY=-10 EndZ=0
    g3: LineSegment StartX=-5 StartY=20.7665 StartZ=0 EndX=-5 EndY=48 EndZ=0
    g4: LineSegment StartX=-3 StartY=50 StartZ=0 EndX=3 EndY=50 EndZ=0
    g5: LineSegment StartX=5 StartY=48 StartZ=0 EndX=5 EndY=20.7665 EndZ=0
    g6: ArcOfCircle CenterX=-13.5 CenterY=-7.5 CenterZ=0 NormalX=0 NormalY=0 NormalZ=1 AngleXU=0 Radius=2.5 StartAngle=3.14159 EndAngle=4.71239
    g7: GeomPoint X=-16 Y=-10 Z=0
    g8: ArcOfCircle CenterX=13.5 CenterY=-7.5 CenterZ=0 NormalX=0 NormalY=0 NormalZ=1 AngleXU=0 Radius=2.5 StartAngle=4.71239 EndAngle=6.28319
    g9: GeomPoint X=16 Y=-10 Z=0
    g10: ArcOfCircle CenterX=13.5 CenterY=7.5 CenterZ=0 NormalX=0 NormalY=0 NormalZ=1 AngleXU=0 Radius=2.5 StartAngle=0 EndAngle=1.38454
    g11: ArcOfCircle CenterX=16 CenterY=20.7665 CenterZ=0 NormalX=0 NormalY=0 NormalZ=1 AngleXU=0 Radius=11 StartAngle=3.14159 EndAngle=4.52613
    g12: ArcOfCircle CenterX=-16 CenterY=20.7665 CenterZ=0 NormalX=0 NormalY=0 NormalZ=1 AngleXU=0 Radius=11 StartAngle=4.89865 EndAngle=6.28319
    g13: ArcOfCircle CenterX=-13.5 CenterY=7.5 CenterZ=0 NormalX=0 NormalY=0 NormalZ=1 AngleXU=0 Radius=2.5 StartAngle=1.75706 EndAngle=3.14159
    g14: ArcOfCircle CenterX=-3 CenterY=48 CenterZ=0 NormalX=0 NormalY=0 NormalZ=1 AngleXU=0 Radius=2 StartAngle=1.5708 EndAngle=3.14159
    g15: GeomPoint X=-5 Y=50 Z=0
    g16: ArcOfCircle CenterX=3 CenterY=48 CenterZ=0 NormalX=0 NormalY=0 NormalZ=1 AngleXU=0 Radius=2 StartAngle=-2.771e-13 EndAngle=1.5708
    g17: GeomPoint X=5 Y=50 Z=0
  constraints (39):
    c: PointOnObject(g7,g0)
    c: PointOnObject(g7,g2)
    c: Tangent(g0,g6) = 1.5708
    c: Tangent(g2,g6) = 1.5708
    c: PointOnObject(g9,g2)
    c: PointOnObject(g9,g1)
    c: Tangent(g2,g8) = 1.5708
    c: Tangent(g1,g8) = 1.5708
    c: Tangent(g1,g10) = 1.5708
    c: Tangent(g5,g11) = -1.5708
    c: Tangent(g3,g12) = -1.5708
    c: Tangent(g0,g13) = 1.5708
    c: PointOnObject(g15,g3)
    c: PointOnObject(g15,g4)
    c: Tangent(g3,g14) = 1.5708
    c: Tangent(g4,g14) = 1.5708
    c: PointOnObject(g17,g4)
    c: PointOnObject(g17,g5)
    c: Tangent(g4,g16) = 1.5708
    c: Tangent(g5,g16) = 1.5708
    c: Equal(g6,g13)
    c: Equal(g6,g8)
    c: Equal(g14,g16)
    c: Tangent(g13,g12) = 1.5708
    c: Tangent(g10,g11) = 1.5708
    c: PointOnObject(g12,g0)
    c: Radius(g14) = 2
    c: Radius(g6) = 2.5
    c: Symmetric(g14,g16,g-2)
    c: Symmetric(g6,g8,g-2)
    c: Symmetric(g13,g6,g-1)
    c: Symmetric(g13,g10,g-2)
    c: DistanceX(g14,g16) = 6
    c: DistanceY(g14) = 48
    c: Symmetric(g12,g11,g-2)
    c: DistanceY(g6,g13) = 15
    c: DistanceX(g6,g8) = 27
    c: Vertical(g3)
    c: Equal(g6,g10)
FEATURE [Sketcher::SketchObject] Sketch001
  AttachmentOffset = pos=(0,0,7) rot=(0,0,1;0rad)
  FullyConstrained = true
  MapMode = 5
  Placement = pos=(0,0,7) rot=(0,0,1;0rad)
  Support = -> [XY_Plane001]
  expr: .AttachmentOffset.Base.z = <<Variables>>.CarriageThickness
  expr: Constraints[26] = Sketch.Constraints[26] - 1mm
  expr: Constraints[27] = Sketch.Constraints[27] - 1mm
  expr: Constraints[32] = Sketch.Constraints[32]
  expr: Constraints[33] = Sketch.Constraints[33]
  expr: Constraints[35] = Sketch.Constraints[35]
  expr: Constraints[36] = Sketch.Constraints[36]
  sketch-geometry (18):
    g0: LineSegment StartX=-15 StartY=-7.5 StartZ=0 EndX=-15 EndY=7.5 EndZ=0
    g1: LineSegment StartX=15 StartY=7.5 StartZ=0 EndX=15 EndY=-7.5 EndZ=0
    g2: LineSegment StartX=13.5 StartY=-9 StartZ=0 EndX=-13.5 EndY=-9 EndZ=0
    g3: LineSegment StartX=-4 StartY=19.9097 StartZ=0 EndX=-4 EndY=48 EndZ=0
    g4: LineSegment StartX=-3 StartY=49 StartZ=0 EndX=3 EndY=49 EndZ=0
    g5: LineSegment StartX=4 StartY=48 StartZ=0 EndX=4 EndY=19.9097 EndZ=0
    g6: ArcOfCircle CenterX=-13.5 CenterY=-7.5 CenterZ=0 NormalX=0 NormalY=0 NormalZ=1 AngleXU=0 Radius=1.5 StartAngle=3.14159 EndAngle=4.71239
    g7: GeomPoint X=-15 Y=-9 Z=0
    g8: ArcOfCircle CenterX=13.5 CenterY=-7.5 CenterZ=0 NormalX=0 NormalY=0 NormalZ=1 AngleXU=0 Radius=1.5 StartAngle=4.71239 EndAngle=6.28319
    g9: GeomPoint X=15 Y=-9 Z=0
    g10: ArcOfCircle CenterX=13.5 CenterY=7.5 CenterZ=0 NormalX=0 NormalY=0 NormalZ=1 AngleXU=0 Radius=1.5 StartAngle=1e-16 EndAngle=1.45051
    g11: ArcOfCircle CenterX=15 CenterY=19.9097 CenterZ=0 NormalX=0 NormalY=0 NormalZ=1 AngleXU=0 Radius=11 StartAngle=3.14159 EndAngle=4.5921
    g12: ArcOfCircle CenterX=-15 CenterY=19.9097 CenterZ=0 NormalX=0 NormalY=0 NormalZ=1 AngleXU=0 Radius=11 StartAngle=4.83268 EndAngle=6.28319
    g13: ArcOfCircle CenterX=-13.5 CenterY=7.5 CenterZ=0 NormalX=0 NormalY=0 NormalZ=1 AngleXU=0 Radius=1.5 StartAngle=1.69109 EndAngle=3.14159
    g14: ArcOfCircle CenterX=-3 CenterY=48 CenterZ=0 NormalX=0 NormalY=0 NormalZ=1 AngleXU=0 Radius=1 StartAngle=1.5708 EndAngle=3.14159
    g15: GeomPoint X=-4 Y=49 Z=0
    g16: ArcOfCircle CenterX=3 CenterY=48 CenterZ=0 NormalX=0 NormalY=0 NormalZ=1 AngleXU=0 Radius=1 StartAngle=1e-16 EndAngle=1.5708
    g17: GeomPoint X=4 Y=49 Z=0
  constraints (39):
    c: PointOnObject(g7,g0)
    c: PointOnObject(g7,g2)
    c: Tangent(g0,g6) = 1.5708
    c: Tangent(g2,g6) = 1.5708
    c: PointOnObject(g9,g2)
    c: PointOnObject(g9,g1)
    c: Tangent(g2,g8) = 1.5708
    c: Tangent(g1,g8) = 1.5708
    c: Tangent(g1,g10) = 1.5708
    c: Tangent(g5,g11) = -1.5708
    c: Tangent(g3,g12) = -1.5708
    c: Tangent(g0,g13) = 1.5708
    c: PointOnObject(g15,g3)
    c: PointOnObject(g15,g4)
    c: Tangent(g3,g14) = 1.5708
    c: Tangent(g4,g14) = 1.5708
    c: PointOnObject(g17,g4)
    c: PointOnObject(g17,g5)
    c: Tangent(g4,g16) = 1.5708
    c: Tangent(g5,g16) = 1.5708
    c: Equal(g6,g13)
    c: Equal(g6,g8)
    c: Equal(g14,g16)
    c: Tangent(g13,g12) = 1.5708
    c: Tangent(g10,g11) = 1.5708
    c: PointOnObject(g12,g0)
    c: Radius(g14) = 1
    c: Radius(g6) = 1.5
    c: Symmetric(g14,g16,g-2)
    c: Symmetric(g6,g8,g-2)
    c: Symmetric(g13,g6,g-1)
    c: Symmetric(g13,g10,g-2)
    c: DistanceX(g14,g16) = 6
    c: DistanceY(g14) = 48
    c: Symmetric(g12,g11,g-2)
    c: DistanceY(g6,g13) = 15
    c: DistanceX(g6,g8) = 27
    c: Vertical(g3)
    c: Equal(g6,g10)
FEATURE [PartDesign::Pad] Pad
  Direction = (0,0,1)
  Length = 6
  Length2 = 10
  Profile = -> Sketch
  ReferenceAxis = -> Sketch [N_Axis]
  Reversed = true
  Type = 0
  expr: Length = <<Variables>>.CarriageThickness - 1
FEATURE [PartDesign::AdditiveLoft] AdditiveLoft
  BaseFeature = -> Pad
  Closed = false
  Profile = -> Sketch
  Ruled = false
  Sections = -> [Sketch001]
FEATURE [Sketcher::SketchObject] Sketch002
  AttachmentOffset = pos=(0,0,7) rot=(0,0,1;0rad)
  FullyConstrained = true
  MapMode = 5
  Placement = pos=(0,0,7) rot=(0,0,1;0rad)
  Support = -> [XY_Plane001]
  expr: .AttachmentOffset.Base.z = <<Variables>>.CarriageThickness
  sketch-geometry (4):
    g0: Circle CenterX=-5 CenterY=7.5 CenterZ=0 NormalX=0 NormalY=0 NormalZ=1 AngleXU=0 Radius=1.5
    g1: Circle CenterX=5 CenterY=7.5 CenterZ=0 NormalX=0 NormalY=0 NormalZ=1 AngleXU=0 Radius=1.5
    g2: Circle CenterX=-5 CenterY=-7.5 CenterZ=0 NormalX=0 NormalY=0 NormalZ=1 AngleXU=0 Radius=1.5
    g3: Circle CenterX=5 CenterY=-7.5 CenterZ=0 NormalX=0 NormalY=0 NormalZ=1 AngleXU=0 Radius=1.5
  constraints (9):
    c: Symmetric(g0,g1,g-2)
    c: Symmetric(g0,g2,g-1)
    c: Symmetric(g1,g3,g-1)
    c: Equal(g0,g1)
    c: Equal(g0,g2)
    c: Equal(g0,g3)
    c: Diameter(g0) = 3
    c: DistanceX(g0,g1) = 10
    c: DistanceY(g2,g0) = 15
FEATURE [PartDesign::Body] Body005  label="CarriageRightBrace"
  Origin = -> Origin009
FEATURE [Sketcher::SketchObject] Sketch003  label="SketchIdlerHole"
  AttachmentOffset = pos=(0,0,-1) rot=(0,0,1;0rad)
  FullyConstrained = true
  MapMode = 5
  Placement = pos=(0,0,-1) rot=(0,0,1;0rad)
  Support = -> [XY_Plane011]
  expr: Constraints[2] = <<Variables>>.IdlerDiameter
  sketch-geometry (2):
    g0: Circle CenterX=0 CenterY=0 CenterZ=0 NormalX=0 NormalY=0 NormalZ=1 AngleXU=0 Radius=1.25
    g1: Circle CenterX=0 CenterY=12.73 CenterZ=0 NormalX=0 NormalY=0 NormalZ=1 AngleXU=0 Radius=1.25
  constraints (5):
    c: Coincident(g0,g-1)
    c: PointOnObject(g1,g-2)
    c: DistanceY(g1) = 12.73
    c: Equal(g1,g0)
    c: Diameter(g1) = 2.5
FEATURE [PartDesign::Hole] Hole
  BaseFeature = -> AdditiveLoft
  CustomThreadClearance = 0
  Depth = 25
  DepthType = 0
  Diameter = 3.4
  DrillForDepth = false
  DrillPoint = 1
  DrillPointAngle = 118
  HoleCutCountersinkAngle = 90
  HoleCutCustomValues = false
  HoleCutDepth = 3
  HoleCutDiameter = 5.7
  HoleCutType = 1
  ModelThread = false
  Profile = -> Sketch002
  Tapered = false
  TaperedAngle = 90
  ThreadClass = 0
  ThreadDepth = 25
  ThreadDepthType = 0
  ThreadDirection = 0
  ThreadFit = 0
  ThreadSize = 9
  ThreadType = 1
  Threaded = false
  UseCustomThreadClearance = false
FEATURE [Sketcher::SketchObject] Sketch004
  FullyConstrained = true
  MapMode = 5
  Support = -> [XY_Plane001]
  sketch-geometry (2):
    g0: Circle CenterX=0 CenterY=20 CenterZ=0 NormalX=0 NormalY=0 NormalZ=1 AngleXU=0 Radius=1.5
    g1: Circle CenterX=0 CenterY=40 CenterZ=0 NormalX=0 NormalY=0 NormalZ=1 AngleXU=0 Radius=1.5
  constraints (6):
    c: PointOnObject(g1,g-2)
    c: PointOnObject(g0,g-2)
    c: Equal(g1,g0)
    c: Diameter(g1) = 3
    c: DistanceY(g0) = 20
    c: DistanceY(g0,g1) = 20
FEATURE [PartDesign::Hole] Hole001
  BaseFeature = -> Hole
  CustomThreadClearance = 0
  Depth = 25
  DepthType = 0
  Diameter = 2.5
  DrillForDepth = false
  DrillPoint = 1
  DrillPointAngle = 118
  HoleCutCountersinkAngle = 90
  HoleCutCustomValues = false
  HoleCutDepth = 0
  HoleCutDiameter = 6.1
  HoleCutType = 0
  ModelThread = false
  Profile = -> Sketch004
  Reversed = true
  Tapered = false
  TaperedAngle = 90
  ThreadClass = 0
  ThreadDepth = 25
  ThreadDepthType = 0
  ThreadDirection = 0
  ThreadFit = 0
  ThreadSize = 9
  ThreadType = 1
  Threaded = true
  UseCustomThreadClearance = false
FEATURE [Sketcher::SketchObject] Sketch005
  FullyConstrained = true
  MapMode = 5
  Support = -> [XY_Plane004]
  sketch-geometry (12):
    g0: LineSegment StartX=-2 StartY=16 StartZ=0 EndX=2 EndY=16 EndZ=0
    g1: LineSegment StartX=5 StartY=13 StartZ=0 EndX=5 EndY=12.5 EndZ=0
    g2: LineSegment StartX=2 StartY=9.5 StartZ=0 EndX=-2 EndY=9.5 EndZ=0
    g3: LineSegment StartX=-5 StartY=12.5 StartZ=0 EndX=-5 EndY=13 EndZ=0
    g4: ArcOfCircle CenterX=-2 CenterY=13 CenterZ=0 NormalX=0 NormalY=0 NormalZ=1 AngleXU=0 Radius=3 StartAngle=1.5708 EndAngle=3.14159
    g5: GeomPoint X=-5 Y=16 Z=0
    g6: ArcOfCircle CenterX=2 CenterY=13 CenterZ=0 NormalX=0 NormalY=0 NormalZ=1 AngleXU=0 Radius=3 StartAngle=0 EndAngle=1.5708
    g7: GeomPoint X=5 Y=16 Z=0
    g8: ArcOfCircle CenterX=-2 CenterY=12.5 CenterZ=0 NormalX=0 NormalY=0 NormalZ=1 AngleXU=0 Radius=3 StartAngle=3.14159 EndAngle=4.71239
    g9: GeomPoint X=-5 Y=9.5 Z=0
    g10: ArcOfCircle CenterX=2 CenterY=12.5 CenterZ=0 NormalX=0 NormalY=0 NormalZ=1 AngleXU=0 Radius=3 StartAngle=4.71239 EndAngle=6.28319
    g11: GeomPoint X=5 Y=9.5 Z=0
  constraints (27):
    c: Horizontal(g0)
    c: Vertical(g1)
    c: Vertical(g3)
    c: PointOnObject(g5,g0)
    c: PointOnObject(g5,g3)
    c: Tangent(g0,g4) = 1.5708
    c: Tangent(g3,g4) = 1.5708
    c: PointOnObject(g7,g0)
    c: PointOnObject(g7,g1)
    c: Tangent(g0,g6) = 1.5708
    c: Tangent(g1,g6) = 1.5708
    c: PointOnObject(g9,g2)
    c: PointOnObject(g9,g3)
    c: Tangent(g2,g8) = 1.5708
    c: Tangent(g3,g8) = 1.5708
    c: PointOnObject(g11,g2)
    c: PointOnObject(g11,g1)
    c: Tangent(g2,g10) = 1.5708
    c: Tangent(g1,g10) = 1.5708
    c: Equal(g4,g6)
    c: Equal(g4,g10)
    c: Equal(g4,g8)
    c: Radius(g4) = 3
    c: DistanceY(g9,g5) = 6.5
    c: Symmetric(g9,g11,g-2)
    c: DistanceX(g9,g11) = 10
    c: DistanceY(g9) = 9.5
FEATURE [PartDesign::Pad] Pad001
  Direction = (0,0,1)
  Length = 16.5
  Length2 = 10
  Profile = -> Sketch005
  ReferenceAxis = -> Sketch005 [N_Axis]
  Type = 0
  expr: Length = <<Variables>>.CarriageThickness + <<Variables>>.WasherThickness * 2 + <<Variables>>.IdlerHeight
FEATURE [Sketcher::SketchObject] Sketch006
  FullyConstrained = true
  MapMode = 5
  Support = -> [XY_Plane008]
  sketch-geometry (12):
    g0: LineSegment StartX=-2 StartY=3.25 StartZ=0 EndX=2 EndY=3.25 EndZ=0
    g1: LineSegment StartX=5 StartY=0.25 StartZ=0 EndX=5 EndY=-0.25 EndZ=0
    g2: LineSegment StartX=2 StartY=-3.25 StartZ=0 EndX=-2 EndY=-3.25 EndZ=0
    g3: LineSegment StartX=-5 StartY=-0.25 StartZ=0 EndX=-5 EndY=0.25 EndZ=0
    g4: ArcOfCircle CenterX=-2 CenterY=0.25 CenterZ=0 NormalX=0 NormalY=0 NormalZ=1 AngleXU=0 Radius=3 StartAngle=1.5708 EndAngle=3.14159
    g5: GeomPoint X=-5 Y=3.25 Z=0
    g6: ArcOfCircle CenterX=2 CenterY=0.25 CenterZ=0 NormalX=0 NormalY=0 NormalZ=1 AngleXU=0 Radius=3 StartAngle=0 EndAngle=1.5708
    g7: GeomPoint X=5 Y=3.25 Z=0
    g8: ArcOfCircle CenterX=-2 CenterY=-0.25 CenterZ=0 NormalX=0 NormalY=0 NormalZ=1 AngleXU=0 Radius=3 StartAngle=3.14159 EndAngle=4.71239
    g9: GeomPoint X=-5 Y=-3.25 Z=0
    g10: ArcOfCircle CenterX=2 CenterY=-0.25 CenterZ=0 NormalX=0 NormalY=0 NormalZ=1 AngleXU=0 Radius=3 StartAngle=4.71239 EndAngle=6.28319
    g11: GeomPoint X=5 Y=-3.25 Z=0
  constraints (27):
    c: Horizontal(g0)
    c: Horizontal(g2)
    c: Vertical(g1)
    c: Vertical(g3)
    c: PointOnObject(g5,g0)
    c: PointOnObject(g5,g3)
    c: Tangent(g0,g4) = 1.5708
    c: Tangent(g3,g4) = 1.5708
    c: PointOnObject(g7,g0)
    c: PointOnObject(g7,g1)
    c: Tangent(g0,g6) = 1.5708
    c: Tangent(g1,g6) = 1.5708
    c: PointOnObject(g9,g2)
    c: PointOnObject(g9,g3)
    c: Tangent(g2,g8) = 1.5708
    c: Tangent(g3,g8) = 1.5708
    c: PointOnObject(g11,g2)
    c: PointOnObject(g11,g1)
    c: Tangent(g2,g10) = 1.5708
    c: Tangent(g1,g10) = 1.5708
    c: Equal(g4,g6)
    c: Equal(g4,g10)
    c: Equal(g4,g8)
    c: Radius(g4) = 3
    c: Symmetric(g5,g11,g-1)
    c: DistanceY(g9,g5) = 6.5
    c: DistanceX(g5,g7) = 10
FEATURE [PartDesign::Pad] Pad002
  Direction = (0,0,1)
  Length = 16.5
  Length2 = 10
  Profile = -> Sketch006
  ReferenceAxis = -> Sketch006 [N_Axis]
  Type = 0
  expr: Length = <<Variables>>.CarriageThickness + <<Variables>>.WasherThickness * 2 + <<Variables>>.IdlerHeight
FEATURE [Sketcher::SketchObject] Sketch007
  AttachmentOffset = pos=(0,0,3) rot=(0,0,1;0rad)
  FullyConstrained = true
  MapMode = 5
  Placement = pos=(0,0,3) rot=(0,0,1;0rad)
  Support = -> [XY_Plane012]
  expr: Constraints[9] = <<Variables>>.IdlerDiameter
  sketch-geometry (4):
    g0: ArcOfCircle CenterX=0 CenterY=0 CenterZ=0 NormalX=0 NormalY=0 NormalZ=1 AngleXU=0 Radius=3.5 StartAngle=1.71414 EndAngle=7.71063
    g1: ArcOfCircle CenterX=-2.1e-15 CenterY=12.73 CenterZ=0 NormalX=0 NormalY=0 NormalZ=1 AngleXU=0 Radius=3.5 StartAngle=4.85574 EndAngle=10.8522
    g2: LineSegment StartX=-0.5 StartY=9.2659 StartZ=0 EndX=-0.5 EndY=3.4641 EndZ=0
    g3: LineSegment StartX=0.5 StartY=9.2659 StartZ=0 EndX=0.5 EndY=3.4641 EndZ=0
  constraints (12):
    c: Coincident(g2,g1)
    c: Coincident(g2,g0)
    c: Coincident(g3,g1)
    c: Coincident(g3,g0)
    c: Coincident(g0,g-1)
    c: Symmetric(g1,g1,g-2)
    c: Symmetric(g0,g0,g-2)
    c: Equal(g1,g0)
    c: Diameter(g1) = 7
    c: DistanceY(g1) = 12.73
    c: DistanceX(g1,g1) = 1
    c: Vertical(g2)
FEATURE [PartDesign::Pad] Pad003
  Direction = (0,0,1)
  Length = 0.2
  Length2 = 10
  Profile = -> Sketch007
  ReferenceAxis = -> Sketch007 [N_Axis]
  Type = 0
FEATURE [PartDesign::Body] Body007  label="IdlerNutHoleSupport"
  Group = -> [Pad003,Sketch007]
  Origin = -> Origin012
  Tip = -> Pad003
FEATURE [Sketcher::SketchObject] Sketch008
  AttachmentOffset = pos=(0,0,-1) rot=(0,0,1;0rad)
  FullyConstrained = true
  MapMode = 5
  Placement = pos=(0,0,-1) rot=(0,0,1;0rad)
  Support = -> [XY_Plane011]
  expr: Constraints[8] = <<Variables>>.IdlerDiameter
  sketch-geometry (4):
    g0: ArcOfCircle CenterX=0 CenterY=0 CenterZ=0 NormalX=0 NormalY=0 NormalZ=1 AngleXU=0 Radius=1.5 StartAngle=3.14159 EndAngle=6.28319
    g1: ArcOfCircle CenterX=0 CenterY=12.73 CenterZ=0 NormalX=0 NormalY=0 NormalZ=1 AngleXU=0 Radius=1.5 StartAngle=2e-16 EndAngle=3.14159
    g2: LineSegment StartX=-1.5 StartY=12.73 StartZ=0 EndX=-1.5 EndY=0 EndZ=0
    g3: LineSegment StartX=1.5 StartY=12.73 StartZ=0 EndX=1.5 EndY=0 EndZ=0
  constraints (9):
    c: Coincident(g0,g-1)
    c: PointOnObject(g1,g-2)
    c: Tangent(g1,g2) = -1.5708
    c: Tangent(g1,g3) = 1.5708
    c: Tangent(g2,g0) = -1.5708
    c: Tangent(g3,g0) = 1.5708
    c: Equal(g0,g1)
    c: Diameter(g0) = 3
    c: DistanceY(g1) = 12.73
FEATURE [PartDesign::Pad] Pad004
  Direction = (0,0,1)
  Length = 0.2
  Length2 = 10
  Profile = -> Sketch008
  ReferenceAxis = -> Sketch008 [N_Axis]
  Reversed = true
  Type = 0
FEATURE [PartDesign::Pad] Pad005
  BaseFeature = -> Pad004
  Direction = (0,0,1)
  Length = 30
  Length2 = 10
  Profile = -> Sketch003
  ReferenceAxis = -> Sketch003 [N_Axis]
  Type = 0
FEATURE [PartDesign::AdditivePrism] Prism
  AttacherType = Attacher::AttachEngine3D
  AttachmentOffset = pos=(0,0,0) rot=(0,0,1;1.5708rad)
  BaseFeature = -> Pad005
  Circumradius = 3.35
  FirstAngle = 0
  Height = 3
  MapMode = 2
  Placement = pos=(0,0,0) rot=(0,0,1;1.5708rad)
  Polygon = 6
  SecondAngle = 0
  Support = -> [X_Axis011]
FEATURE [PartDesign::AdditivePrism] Prism001
  AttacherType = Attacher::AttachEngine3D
  AttachmentOffset = pos=(0,12.73,0) rot=(0,0,1;1.5708rad)
  BaseFeature = -> Prism
  Circumradius = 3.35
  FirstAngle = 0
  Height = 3
  MapMode = 2
  Placement = pos=(0,12.73,0) rot=(0,0,1;1.5708rad)
  Polygon = 6
  SecondAngle = 0
  Support = -> [X_Axis011]
  expr: .AttachmentOffset.Base.y = <<Variables>>.IdlerDiameter
FEATURE [PartDesign::Body] Body006  label="IdlerNutHoles"
  Group = -> [Pad004,Pad005,Prism,Sketch003,Sketch008,Prism001]
  Origin = -> Origin011
  Tip = -> Prism001
FEATURE [Sketcher::SketchObject] Sketch009
  AttachmentOffset = pos=(0,0,8) rot=(0,0,1;0rad)
  FullyConstrained = true
  MapMode = 5
  Placement = pos=(0,0,8) rot=(0,0,1;0rad)
  Support = -> [XY_Plane013]
  expr: .AttachmentOffset.Base.z = <<Variables>>.CarriageThickness + 1
  sketch-geometry (4):
    g0: ArcOfCircle CenterX=0 CenterY=40 CenterZ=0 NormalX=0 NormalY=0 NormalZ=1 AngleXU=0 Radius=1.5 StartAngle=-1.91456e-11 EndAngle=3.14159
    g1: ArcOfCircle CenterX=0 CenterY=20 CenterZ=0 NormalX=0 NormalY=0 NormalZ=1 AngleXU=0 Radius=1.5 StartAngle=3.14159 EndAngle=6.28319
    g2: LineSegment StartX=-1.5 StartY=40 StartZ=0 EndX=-1.5 EndY=20 EndZ=0
    g3: LineSegment StartX=1.5 StartY=20 StartZ=0 EndX=1.5 EndY=40 EndZ=0
  constraints (10):
    c: PointOnObject(g0,g-2)
    c: PointOnObject(g1,g-2)
    c: Tangent(g2,g0) = -1.5708
    c: Tangent(g0,g3) = -1.5708
    c: Tangent(g2,g1) = -1.5708
    c: Tangent(g3,g1) = -1.5708
    c: Equal(g0,g1)
    c: Diameter(g0) = 3
    c: DistanceY(g1) = 20
    c: DistanceY(g1,g0) = 20
FEATURE [PartDesign::Pad] Pad006
  Direction = (0,0,1)
  Length = 0.2
  Length2 = 10
  Profile = -> Sketch009
  ReferenceAxis = -> Sketch009 [N_Axis]
  Type = 0
FEATURE [PartDesign::AdditivePrism] Prism003
  AttacherType = Attacher::AttachEngine3D
  AttachmentOffset = pos=(0,20,8) rot=(0.707107,0.707107,0;3.14159rad)
  BaseFeature = -> Pad006
  Circumradius = 3.35
  FirstAngle = 0
  Height = 4
  MapMode = 2
  Placement = pos=(0,20,8) rot=(0.707107,0.707107,0;3.14159rad)
  Polygon = 6
  SecondAngle = 0
  Support = -> [X_Axis013]
  expr: .AttachmentOffset.Base.z = <<Variables>>.CarriageThickness + 1
FEATURE [PartDesign::AdditivePrism] Prism004
  AttacherType = Attacher::AttachEngine3D
  AttachmentOffset = pos=(0,40,8) rot=(0.707107,0.707107,0;3.14159rad)
  BaseFeature = -> Prism003
  Circumradius = 3.35
  FirstAngle = 0
  Height = 4
  MapMode = 2
  Placement = pos=(0,40,8) rot=(0.707107,0.707107,0;3.14159rad)
  Polygon = 6
  SecondAngle = 0
  Support = -> [X_Axis013]
  expr: .AttachmentOffset.Base.z = <<Variables>>.CarriageThickness + 1
FEATURE [PartDesign::Body] Body008  label="RailNutHoles"
  Group = -> [Sketch009,Pad006,Prism003,Prism004]
  Origin = -> Origin013
  Tip = -> Prism004
FEATURE [PartDesign::Boolean] Boolean
  BaseFeature = -> Hole001
  Group = -> [Body008]
  Type = 1
FEATURE [PartDesign::Body] Body  label="CarriageBaseMain"
  Group = -> [Sketch,Sketch001,Pad,AdditiveLoft,Sketch002,Hole,Sketch004,Hole001,Boolean]
  Origin = -> Origin001
  Tip = -> Boolean
FEATURE [App::Part] Part  label="CarriageBase"
  Group = -> [Body,Body001,Body007,Body006]
  Origin = -> Origin
FEATURE [Part::FeaturePython] Clone004  label="CarriageBaseMain001"  # Draft clone (typed FeaturePython)
  AttacherType = Attacher::AttachEngine3D
  Fuse = false
  Objects = -> [Body]
  Scale = (1,1,1)
FEATURE [PartDesign::Boolean] Boolean001
  BaseFeature = -> Pad001
  Group = -> [Clone004]
  Type = 0
FEATURE [Part::FeaturePython] Clone005  label="CarriageBaseMain002"  # Draft clone (typed FeaturePython)
  AttacherType = Attacher::AttachEngine3D
  Fuse = false
  Objects = -> [Body]
  Scale = (1,1,1)
FEATURE [PartDesign::Boolean] Boolean002
  BaseFeature = -> Pad002
  Group = -> [Clone005]
  Type = 0
FEATURE [PartDesign::ShapeBinder] ShapeBinder
  Support = -> [Body007]
  TraceSupport = false
FEATURE [PartDesign::ShapeBinder] ShapeBinder001
  Support = -> [Body006]
  TraceSupport = false
FEATURE [PartDesign::Boolean] Boolean003
  BaseFeature = -> Boolean001
  Group = -> [ShapeBinder001]
  Type = 1
FEATURE [PartDesign::Boolean] Boolean004
  BaseFeature = -> Boolean003
  Group = -> [ShapeBinder]
  Refine = true
  Type = 0
FEATURE [PartDesign::Body] Body002  label="CarriageLeftMain"
  Group = -> [Sketch005,Pad001,Boolean001,Boolean003,Boolean004]
  Origin = -> Origin004
  Tip = -> Boolean004
FEATURE [PartDesign::ShapeBinder] ShapeBinder002
  Support = -> [Body007]
  TraceSupport = false
FEATURE [PartDesign::ShapeBinder] ShapeBinder003
  Support = -> [Body006]
  TraceSupport = false
FEATURE [PartDesign::Boolean] Boolean005
  BaseFeature = -> Boolean002
  Group = -> [ShapeBinder003]
  Type = 1
FEATURE [PartDesign::Boolean] Boolean006
  BaseFeature = -> Boolean005
  Group = -> [ShapeBinder002]
  Refine = true
  Type = 0
FEATURE [PartDesign::Body] Body004  label="CarriageRightMain"
  Group = -> [Sketch006,Pad002,Boolean002,Boolean005,Boolean006]
  Origin = -> Origin008
  Tip = -> Boolean006
FEATURE [PartDesign::CoordinateSystem] LCS_CarriageLeftOrigin
  AttacherType = Attacher::AttachEngine3D
  AttachmentOffset = pos=(0,0,0) rot=(0,0,1;1.5708rad)
  MapMode = 2
  Placement = pos=(0,0,0) rot=(0,0,1;1.5708rad)
  Support = -> [X_Axis003]
FEATURE [App::Part] Part001  label="CarriageLeft"
  Group = -> [Body002,Body003,LCS_CarriageLeftOrigin]
  Origin = -> Origin003
FEATURE [PartDesign::CoordinateSystem] LCS_CarriageRightOrigin
  AttacherType = Attacher::AttachEngine3D
  AttachmentOffset = pos=(0,0,0) rot=(0,0,-1;1.5708rad)
  MapMode = 2
  Placement = pos=(0,0,0) rot=(0,0,-1;1.5708rad)
  Support = -> [X_Axis007]
FEATURE [App::Part] Part002  label="CarriageRight"
  Group = -> [Body004,Body005,LCS_CarriageRightOrigin]
  Origin = -> Origin007
FEATURE [App::Link] CarriageLeft  label="CarriageLeft001"
  AssemblyType = Part::Link
  AttachedBy = #LCS_CarriageLeftOrigin
  AttachedTo = CarriageLayout#LCS_CarriageLeftPosition
  LinkPlacement = pos=(-100,0,0) rot=(0,0,-1;1.5708rad)
  LinkedObject = -> Part001
  Placement = pos=(-100,0,0) rot=(0,0,-1;1.5708rad)
  SolverId = Asm4EE
  expr: Placement = CarriageLayout.Placement * LCS_CarriageLeftPosition.Placement * AttachmentOffset * LCS_CarriageLeftOrigin.Placement ^ -1
FEATURE [App::Link] CarriageRight  label="CarriageRight001"
  AssemblyType = Part::Link
  AttachedBy = #LCS_CarriageRightOrigin
  AttachedTo = CarriageLayout#LCS_CarriageRightPosition
  LinkPlacement = pos=(100,0,0) rot=(0,0,1;1.5708rad)
  LinkedObject = -> Part002
  Placement = pos=(100,0,0) rot=(0,0,1;1.5708rad)
  SolverId = Asm4EE
  expr: Placement = CarriageLayout.Placement * LCS_CarriageRightPosition.Placement * AttachmentOffset * LCS_CarriageRightOrigin.Placement ^ -1
FEATURE [PartDesign::CoordinateSystem] LCS_CarriageLayoutOrigin
  AttacherType = Attacher::AttachEngine3D
  MapMode = 2
  Support = -> [X_Axis014]
FEATURE [App::Part] Part003  label="CarriageLayout"
  Group = -> [LCS_CarriageLayoutOrigin,LCS_CarriageLeftPosition,LCS_CarriageRightPosition]
  Origin = -> Origin014
FEATURE [App::DocumentObjectGroup] Parts
  Group = -> [Part,Part001,Part002,Part003]
FEATURE [App::Link] CarriageLayout  label="CarriageLayout001"
  AssemblyType = Part::Link
  AttachedBy = #LCS_CarriageLayoutOrigin
  AttachedTo = Parent Assembly#LCS_Origin
  LinkedObject = -> Part003
  SolverId = Asm4EE
  expr: Placement = LCS_Origin.Placement * AttachmentOffset * LCS_CarriageLayoutOrigin.Placement ^ -1
FEATURE [PartDesign::CoordinateSystem] LCS_LeftOuterIdlerPosition
  AttacherType = Attacher::AttachEngine3D
  AttachmentOffset = pos=(0,0,11.75) rot=(0,0,1;0rad)
  MapMode = 5
  Placement = pos=(-100,0,11.75) rot=(0,0,1;0rad)
  Support = -> [LCS_CarriageLeftPosition]
  expr: .AttachmentOffset.Base.z = <<Variables>>.CarriageThickness + <<Variables>>.WasherThickness + <<Variables>>.IdlerHeight / 2
FEATURE [PartDesign::CoordinateSystem] LCS_LeftInnerIdlerPosition
  AttacherType = Attacher::AttachEngine3D
  AttachmentOffset = pos=(12.73,0,21.25) rot=(0,0,1;0rad)
  MapMode = 5
  Placement = pos=(-87.27,0,21.25) rot=(0,0,1;0rad)
  Support = -> [LCS_CarriageLeftPosition]
  expr: .AttachmentOffset.Base.x = <<Variables>>.IdlerDiameter
  expr: .AttachmentOffset.Base.z = <<Variables>>.CarriageThickness + <<Variables>>.WasherThickness * 3 + <<Variables>>.IdlerHeight * 1.5
FEATURE [PartDesign::CoordinateSystem] LCS_RightOuterIdlerPosition
  AttacherType = Attacher::AttachEngine3D
  AttachmentOffset = pos=(0,0,21.25) rot=(0,0,1;0rad)
  MapMode = 5
  Placement = pos=(100,0,21.25) rot=(0,0,1;0rad)
  Support = -> [LCS_CarriageRightPosition]
  expr: .AttachmentOffset.Base.z = <<Variables>>.CarriageThickness + <<Variables>>.WasherThickness * 3 + <<Variables>>.IdlerHeight * 1.5
FEATURE [PartDesign::CoordinateSystem] LCS_RightInnerIdlerPosition
  AttacherType = Attacher::AttachEngine3D
  AttachmentOffset = pos=(-12.73,0,11.75) rot=(0,0,1;0rad)
  MapMode = 5
  Placement = pos=(87.27,0,11.75) rot=(0,0,1;0rad)
  Support = -> [LCS_CarriageRightPosition]
  expr: .AttachmentOffset.Base.x = -<<Variables>>.IdlerDiameter
  expr: .AttachmentOffset.Base.z = <<Variables>>.CarriageThickness + <<Variables>>.WasherThickness + <<Variables>>.IdlerHeight / 2
FEATURE [App::Part] Model
  AssemblyType = Part::Link
  Group = -> [LCS_Origin,Constraints,Variables,Configurations,CarriageLeft,CarriageRight,CarriageLayout,LCS_LeftOuterIdlerPosition,LCS_LeftInnerIdlerPosition,LCS_RightOuterIdlerPosition,LCS_RightInnerIdlerPosition]
  Origin = -> Origin006
  Type = Assembly
---- part miniXY-ZDrive.FCStd = doc fcstd_499f4646abeb ----
FCSTD DOCUMENT  (FreeCAD 0.20R29177 (Git))
Label: miniXY-ZDrive
License: All rights reserved
LicenseURL: http://en.wikipedia.org/wiki/All_rights_reserved
objects: App::Part×4, App::Link×4, App::DocumentObjectGroup×3, Sketcher::SketchObject×3, PartDesign::Revolution×3, PartDesign::Body×3, PartDesign::CoordinateSystem×1, App::FeaturePython×1
note: 13 computed .brp shape members not serialized (recipe doc carries the construction recipe); baked Part::Feature solids carry a one-line shape summary decoded from their .brp

FEATURE [PartDesign::CoordinateSystem] LCS_Origin
  AttacherType = Attacher::AttachEngine3D
  MapMode = 2
  Support = -> [X_Axis]
FEATURE [App::DocumentObjectGroup] Constraints
FEATURE [App::FeaturePython] Variables  # WARN: FeaturePython — macro-defined, semantics opaque (R4)
  DriveShaftLength = 200
  Pully80TPosition = 60
  PullyDriveDiameter = 12.73
  PullyDrivePosition = 83.5
  Type = App::PropertyContainer
FEATURE [App::DocumentObjectGroup] Configurations
FEATURE [Sketcher::SketchObject] Sketch
  FullyConstrained = true
  MapMode = 5
  Support = -> [XY_Plane004]
  expr: Constraints[21] = -50.93 / 2
  sketch-geometry (10):
    g0: LineSegment StartX=-11 StartY=-2.5 StartZ=0 EndX=-11 EndY=-8 EndZ=0
    g1: LineSegment StartX=-11 StartY=-8 StartZ=0 EndX=-5.5 EndY=-8 EndZ=0
    g2: LineSegment StartX=-5.5 StartY=-8 StartZ=0 EndX=-5.5 EndY=-26.465 EndZ=0
    g3: LineSegment StartX=-5.5 StartY=-26.465 StartZ=0 EndX=-4.5 EndY=-25.465 EndZ=0
    g4: LineSegment StartX=-4.5 StartY=-25.465 StartZ=0 EndX=4.5 EndY=-25.465 EndZ=0
    g5: LineSegment StartX=4.5 StartY=-25.465 StartZ=0 EndX=5.5 EndY=-26.465 EndZ=0
    g6: LineSegment StartX=5.5 StartY=-26.465 StartZ=0 EndX=5.5 EndY=-9 EndZ=0
    g7: LineSegment StartX=5.5 StartY=-9 StartZ=0 EndX=10.5 EndY=-4 EndZ=0
    g8: LineSegment StartX=10.5 StartY=-4 StartZ=0 EndX=10.5 EndY=-2.5 EndZ=0
    g9: LineSegment StartX=10.5 StartY=-2.5 StartZ=0 EndX=-11 EndY=-2.5 EndZ=0
  constraints (28):
    c: Vertical(g0)
    c: Coincident(g0,g1)
    c: Coincident(g1,g2)
    c: Vertical(g2)
    c: Coincident(g2,g3)
    c: Coincident(g3,g4)
    c: Coincident(g4,g5)
    c: Coincident(g5,g6)
    c: Coincident(g6,g7)
    c: Coincident(g7,g8)
    c: Coincident(g8,g9)
    c: Coincident(g9,g0)
    c: Horizontal(g9)
    c: Angle(g3) = 0.785398
    c: Parallel(g3,g7)
    c: Vertical(g6)
    c: Vertical(g8)
    c: Symmetric(g3,g4,g-2)
    c: DistanceX(g4,g4) = 9
    c: Symmetric(g2,g5,g-2)
    c: DistanceX(g2,g3) = 1
    c: DistanceY(g3) = -25.465
    c: Horizontal(g1)
    c: DistanceY(g0) = -2.5
    c: DistanceX(g1,g1) = 5.5
    c: DistanceY(g0) = -8
    c: DistanceX(g7,g7) = 5
    c: DistanceY(g8,g8) = 1.5
FEATURE [PartDesign::Revolution] Revolution
  Angle = 360
  Axis = (1,0,0)
  Base = (0,0,0)
  Profile = -> Sketch
  ReferenceAxis = -> Sketch [H_Axis]
  Reversed = true
FEATURE [PartDesign::Body] Body002  label="Pully80TBody"
  Group = -> [Sketch,Revolution]
  Origin = -> Origin004
  Tip = -> Revolution
FEATURE [App::Part] Part001  label="Pully80T"
  Group = -> [Body002]
  Origin = -> Origin005
FEATURE [Sketcher::SketchObject] Sketch118
  FullyConstrained = true
  MapMode = 5
  Support = -> [XY_Plane003]
  expr: Constraints[18] = -<<Variables>>.PullyDriveDiameter / 2
  sketch-geometry (8):
    g0: LineSegment StartX=-11 StartY=-2.5 StartZ=0 EndX=-11 EndY=-8 EndZ=0
    g1: LineSegment StartX=-11 StartY=-8 StartZ=0 EndX=-3.5 EndY=-8 EndZ=0
    g2: LineSegment StartX=-3.5 StartY=-8 StartZ=0 EndX=-3.5 EndY=-6.365 EndZ=0
    g3: LineSegment StartX=-3.5 StartY=-6.365 StartZ=0 EndX=3.5 EndY=-6.365 EndZ=0
    g4: LineSegment StartX=3.5 StartY=-6.365 StartZ=0 EndX=3.5 EndY=-8 EndZ=0
    g5: LineSegment StartX=3.5 StartY=-8 StartZ=0 EndX=5 EndY=-8 EndZ=0
    g6: LineSegment StartX=5 StartY=-8 StartZ=0 EndX=5 EndY=-2.5 EndZ=0
    g7: LineSegment StartX=5 StartY=-2.5 StartZ=0 EndX=-11 EndY=-2.5 EndZ=0
  constraints (23):
    c: Vertical(g0)
    c: Coincident(g0,g1)
    c: Horizontal(g1)
    c: Coincident(g1,g2)
    c: Coincident(g2,g3)
    c: Coincident(g3,g4)
    c: Vertical(g4)
    c: Coincident(g4,g5)
    c: Coincident(g5,g6)
    c: Vertical(g6)
    c: Coincident(g6,g7)
    c: Coincident(g7,g0)
    c: Horizontal(g7)
    c: Symmetric(g2,g3,g-2)
    c: Vertical(g2)
    c: DistanceX(g7,g7) = 16
    c: DistanceY(g0) = -2.5
    c: DistanceY(g0) = -8
    c: DistanceY(g2) = -6.365
    c: DistanceX(g5,g5) = 1.5
    c: DistanceX(g1,g1) = 7.5
    c: Horizontal(g5)
    c: DistanceY(g5) = -8
FEATURE [PartDesign::Revolution] Revolution001
  Angle = 360
  Axis = (1,0,0)
  Base = (0,0,0)
  Profile = -> Sketch118
  ReferenceAxis = -> Sketch118 [H_Axis]
  Reversed = true
FEATURE [PartDesign::Body] Body001  label="PullyDriveBody"
  Group = -> [Sketch118,Revolution001]
  Origin = -> Origin003
  Tip = -> Revolution001
FEATURE [App::Part] Part002  label="PullyDrive"
  Group = -> [Body001]
  Origin = -> Origin006
FEATURE [Sketcher::SketchObject] Sketch119
  FullyConstrained = true
  MapMode = 5
  Support = -> [XY_Plane002]
  expr: Constraints[13] = <<Variables>>.DriveShaftLength
  sketch-geometry (16):
    g0: LineSegment StartX=-100 StartY=-8 StartZ=0 EndX=-95 EndY=-8 EndZ=0
    g1: LineSegment StartX=-95 StartY=-8 StartZ=0 EndX=-95 EndY=-2.5 EndZ=0
    g2: LineSegment StartX=-95 StartY=-2.5 StartZ=0 EndX=95 EndY=-2.5 EndZ=0
    g3: LineSegment StartX=95 StartY=-2.5 StartZ=0 EndX=95 EndY=-8 EndZ=0
    g4: LineSegment StartX=95 StartY=-8 StartZ=0 EndX=100 EndY=-8 EndZ=0
    g5: LineSegment StartX=100 StartY=0 StartZ=0 EndX=-100 EndY=0 EndZ=0
    g6: LineSegment StartX=-100 StartY=-3.5 StartZ=0 EndX=100 EndY=-3.5 EndZ=0
    g7: LineSegment StartX=-100 StartY=-7 StartZ=0 EndX=100 EndY=-7 EndZ=0
    g8: LineSegment StartX=-100 StartY=0 StartZ=0 EndX=-100 EndY=-2.4 EndZ=0
    g9: LineSegment StartX=-100 StartY=-2.4 StartZ=0 EndX=-99.9 EndY=-2.5 EndZ=0
    g10: LineSegment StartX=-99.9 StartY=-2.5 StartZ=0 EndX=-100 EndY=-2.6 EndZ=0
    g11: LineSegment StartX=99.9 StartY=-2.5 StartZ=0 EndX=100 EndY=-2.4 EndZ=0
    g12: LineSegment StartX=100 StartY=-2.4 StartZ=0 EndX=100 EndY=0 EndZ=0
    g13: LineSegment StartX=100 StartY=-8 StartZ=0 EndX=100 EndY=-2.6 EndZ=0
    g14: LineSegment StartX=100 StartY=-2.6 StartZ=0 EndX=99.9 EndY=-2.5 EndZ=0
    g15: LineSegment StartX=-100 StartY=-2.6 StartZ=0 EndX=-100 EndY=-8 EndZ=0
  constraints (40):
    c: Coincident(g0,g1)
    c: Vertical(g1)
    c: Coincident(g1,g2)
    c: Coincident(g2,g3)
    c: Coincident(g3,g4)
    c: Coincident(g4,g13)
    c: Coincident(g12,g5)
    c: Horizontal(g0)
    c: Symmetric(g5,g12,g-2)
    c: Symmetric(g1,g2,g-2)
    c: Symmetric(g0,g3,g-2)
    c: Symmetric(g0,g4,g-2)
    c: PointOnObject(g5,g-1)
    c: DistanceX(g5,g5) = 200
    c: DistanceY(g0) = -8
    c: DistanceY(g1) = -2.5
    c: DistanceX(g0,g0) = 5
    c: Coincident(g8,g5)
    c: Symmetric(g6,g6,g-2)
    c: Symmetric(g7,g7,g-2)
    c: DistanceY(g6,g1) = 1
    c: Coincident(g9,g10)
    c: Coincident(g8,g9)
    c: Vertical(g8)
    c: Coincident(g10,g15)
    c: PointOnObject(g9,g2)
    c: Symmetric(g8,g10,g2)
    c: Angle(g9) = -0.785398
    c: DistanceY(g10,g8) = 0.2
    c: DistanceY(g0,g7) = 1
    c: Coincident(g14,g11)
    c: Coincident(g11,g12)
    c: Coincident(g13,g14)
    c: Symmetric(g11,g9,g-2)
    c: Symmetric(g8,g11,g-2)
    c: Symmetric(g13,g10,g-2)
    c: Vertical(g15)
    c: PointOnObject(g6,g8)
    c: PointOnObject(g7,g8)
    c: Coincident(g15,g0)
FEATURE [PartDesign::Revolution] Revolution002
  Angle = 360
  Axis = (1,0,0)
  Base = (0,0,0)
  Profile = -> Sketch119
  ReferenceAxis = -> Sketch119 [H_Axis]
  Reversed = true
FEATURE [PartDesign::Body] Body  label="ShaftBody"
  Group = -> [Sketch119,Revolution002]
  Origin = -> Origin002
  Tip = -> Revolution002
FEATURE [App::Part] Part  label="DriveShaft"
  Group = -> [Body]
  Origin = -> Origin001
FEATURE [App::DocumentObjectGroup] Parts
  Group = -> [Part,Part001,Part002]
FEATURE [App::Link] DriveShaft  label="DriveShaft001"
  LinkedObject = -> Part
FEATURE [App::Link] PullyDriveLeft
  LinkPlacement = pos=(-83.5,0,0) rot=(0,0,1;0rad)
  LinkedObject = -> Part002
  Placement = pos=(-83.5,0,0) rot=(0,0,1;0rad)
  expr: .Placement.Base.x = -<<Variables>>.PullyDrivePosition
FEATURE [App::Link] PullyDriveRight
  LinkPlacement = pos=(83.5,0,0) rot=(0,0,1;3.14159rad)
  LinkedObject = -> Part002
  Placement = pos=(83.5,0,0) rot=(0,0,1;3.14159rad)
  expr: .Placement.Base.x = <<Variables>>.PullyDrivePosition
FEATURE [App::Link] Pully80T  label="Pully80T001"
  LinkPlacement = pos=(60,0,0) rot=(0,0,1;0rad)
  LinkedObject = -> Part001
  Placement = pos=(60,0,0) rot=(0,0,1;0rad)
  expr: .Placement.Base.x = <<Variables>>.Pully80TPosition
FEATURE [App::Part] Model
  AssemblyType = Part::Link
  Group = -> [LCS_Origin,Constraints,Variables,Configurations,DriveShaft,PullyDriveLeft,PullyDriveRight,Pully80T]
  Origin = -> Origin
  Type = Assembly
